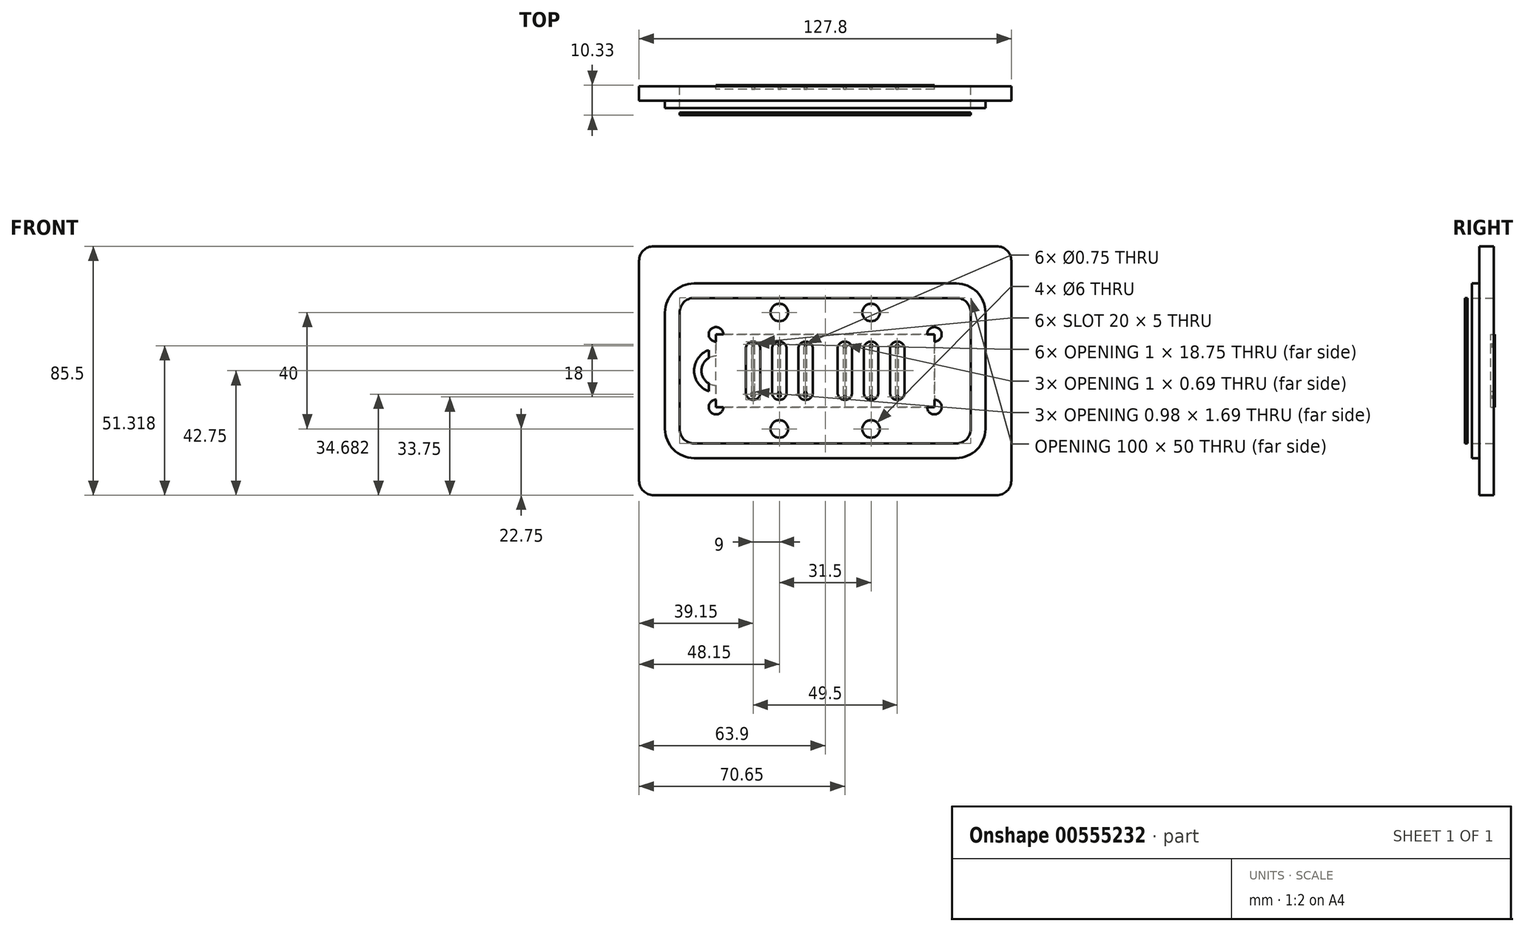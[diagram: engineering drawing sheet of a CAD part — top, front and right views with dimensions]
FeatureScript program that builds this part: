
annotation { "Feature Type Name" : "Feature", "Feature Type Description" : "" }
export const myFeature = defineFeature(function(context is Context, id is Id, definition is map)
    precondition{}
    {
        {
            var Q0;
            Q0=qCreatedBy(makeId("Front.planeOp"),FACE);
            var sketch = newSketch(context, id + "F0", { "sketchPlane" : qUnion([Q0])});
            skLineSegment(sketch, "E0.bottom", {"start": v(-58.9, 42.75) * mm, "end": v(58.9, 42.75) * mm});
            skLineSegment(sketch, "E0.top", {"start": v(-58.9, -42.75) * mm, "end": v(58.9, -42.75) * mm});
            skLineSegment(sketch, "E0.left", {"start": v(-63.9, 37.75) * mm, "end": v(-63.9, -37.75) * mm});
            skLineSegment(sketch, "E0.right", {"start": v(63.9, 37.75) * mm, "end": v(63.9, -37.75) * mm});
            skLineSegment(sketch, "E1.bottom", {"start": v(-37.5, 12.5) * mm, "end": v(37.5, 12.5) * mm});
            skLineSegment(sketch, "E1.top", {"start": v(-37.5, -12.5) * mm, "end": v(37.5, -12.5) * mm});
            skLineSegment(sketch, "E1.left", {"start": v(-37.5, 12.5) * mm, "end": v(-37.5, -12.5) * mm});
            skLineSegment(sketch, "E1.right", {"start": v(37.5, 12.5) * mm, "end": v(37.5, -12.5) * mm});
            skPoint(sketch, "E1.middle", {"position": v(0, 0) * mm});
            skPoint(sketch, "E2.visualSharp", {"position": v(-63.9, 42.75) * mm});
            skArc(sketch, "E2.filletArc", {"start": v(-58.9, 42.75) * mm, "mid": v(-62.44, 41.29) * mm, "end": v(-63.9, 37.75) * mm});
            skPoint(sketch, "E3.visualSharp", {"position": v(63.9, 42.75) * mm});
            skArc(sketch, "E3.filletArc", {"start": v(63.9, 37.75) * mm, "mid": v(62.44, 41.29) * mm, "end": v(58.9, 42.75) * mm});
            skPoint(sketch, "E4.visualSharp", {"position": v(63.9, -42.75) * mm});
            skArc(sketch, "E4.filletArc", {"start": v(58.9, -42.75) * mm, "mid": v(62.44, -41.29) * mm, "end": v(63.9, -37.75) * mm});
            skPoint(sketch, "E5.visualSharp", {"position": v(-63.9, -42.75) * mm});
            skArc(sketch, "E5.filletArc", {"start": v(-63.9, -37.75) * mm, "mid": v(-62.44, -41.29) * mm, "end": v(-58.9, -42.75) * mm});
            skCircle(sketch, "E6", {"center": v(-6.75, 9) * mm, "radius": 3.18 * mm});
            skCircle(sketch, "E7", {"center": v(-15.75, 9) * mm, "radius": 3.18 * mm});
            skCircle(sketch, "E8", {"center": v(-24.75, 9) * mm, "radius": 3.18 * mm});
            skCircle(sketch, "E9", {"center": v(6.75, 9) * mm, "radius": 3.18 * mm});
            skCircle(sketch, "E10", {"center": v(15.75, 9) * mm, "radius": 3.18 * mm});
            skCircle(sketch, "E11", {"center": v(24.75, 9) * mm, "radius": 3.18 * mm});
            skLineSegment(sketch, "E12.bottom", {"start": v(24.75, -10) * mm, "end": v(24.75, -10) * mm});
            skLineSegment(sketch, "E12.top", {"start": v(24.75, 10) * mm, "end": v(24.75, 10) * mm});
            skLineSegment(sketch, "E12.left", {"start": v(27.25, -7.5) * mm, "end": v(27.25, 7.5) * mm});
            skLineSegment(sketch, "E12.right", {"start": v(22.25, -7.5) * mm, "end": v(22.25, 7.5) * mm});
            skLineSegment(sketch, "E13.bottom", {"start": v(15.75, -10) * mm, "end": v(15.75, -10) * mm});
            skLineSegment(sketch, "E13.top", {"start": v(15.75, 10) * mm, "end": v(15.75, 10) * mm});
            skLineSegment(sketch, "E13.left", {"start": v(18.25, -7.5) * mm, "end": v(18.25, 7.5) * mm});
            skLineSegment(sketch, "E13.right", {"start": v(13.25, -7.5) * mm, "end": v(13.25, 7.5) * mm});
            skLineSegment(sketch, "E14.bottom", {"start": v(6.75, -10) * mm, "end": v(6.75, -10) * mm});
            skLineSegment(sketch, "E14.top", {"start": v(6.75, 10) * mm, "end": v(6.75, 10) * mm});
            skLineSegment(sketch, "E14.left", {"start": v(9.25, -7.5) * mm, "end": v(9.25, 7.5) * mm});
            skLineSegment(sketch, "E14.right", {"start": v(4.25, -7.5) * mm, "end": v(4.25, 7.5) * mm});
            skLineSegment(sketch, "E15.bottom", {"start": v(-6.75, -10) * mm, "end": v(-6.75, -10) * mm});
            skLineSegment(sketch, "E15.top", {"start": v(-6.75, 10) * mm, "end": v(-6.75, 10) * mm});
            skLineSegment(sketch, "E15.left", {"start": v(-4.25, -7.5) * mm, "end": v(-4.25, 7.5) * mm});
            skLineSegment(sketch, "E15.right", {"start": v(-9.25, -7.5) * mm, "end": v(-9.25, 7.5) * mm});
            skLineSegment(sketch, "E16.bottom", {"start": v(-15.75, -10) * mm, "end": v(-15.75, -10) * mm});
            skLineSegment(sketch, "E16.top", {"start": v(-15.75, 10) * mm, "end": v(-15.75, 10) * mm});
            skLineSegment(sketch, "E16.left", {"start": v(-13.25, -7.5) * mm, "end": v(-13.25, 7.5) * mm});
            skLineSegment(sketch, "E16.right", {"start": v(-18.25, -7.5) * mm, "end": v(-18.25, 7.5) * mm});
            skLineSegment(sketch, "E17.bottom", {"start": v(-24.75, -10) * mm, "end": v(-24.75, -10) * mm});
            skLineSegment(sketch, "E17.top", {"start": v(-24.75, 10) * mm, "end": v(-24.75, 10) * mm});
            skLineSegment(sketch, "E17.left", {"start": v(-22.25, -7.5) * mm, "end": v(-22.25, 7.5) * mm});
            skLineSegment(sketch, "E17.right", {"start": v(-27.25, -7.5) * mm, "end": v(-27.25, 7.5) * mm});
            skCircle(sketch, "E18", {"center": v(24.75, -9) * mm, "radius": 3.18 * mm});
            skPoint(sketch, "E19", {"position": v(24.75, -10) * mm});
            skCircle(sketch, "E20", {"center": v(15.75, -9) * mm, "radius": 3.18 * mm});
            skPoint(sketch, "E21", {"position": v(15.75, -10) * mm});
            skCircle(sketch, "E22", {"center": v(6.75, -9) * mm, "radius": 3.18 * mm});
            skPoint(sketch, "E23", {"position": v(6.75, -10) * mm});
            skCircle(sketch, "E24", {"center": v(-6.75, -9) * mm, "radius": 3.18 * mm});
            skPoint(sketch, "E25", {"position": v(-6.75, -10) * mm});
            skCircle(sketch, "E26", {"center": v(-15.75, -9) * mm, "radius": 3.18 * mm});
            skPoint(sketch, "E27", {"position": v(-15.75, -10) * mm});
            skCircle(sketch, "E28", {"center": v(-24.75, -9) * mm, "radius": 3.18 * mm});
            skPoint(sketch, "E29", {"position": v(-24.75, -10) * mm});
            skPoint(sketch, "E30.visualSharp", {"position": v(-27.25, 10) * mm});
            skArc(sketch, "E30.filletArc", {"start": v(-24.75, 10) * mm, "mid": v(-26.52, 9.27) * mm, "end": v(-27.25, 7.5) * mm});
            skPoint(sketch, "E31.visualSharp", {"position": v(-22.25, 10) * mm});
            skArc(sketch, "E31.filletArc", {"start": v(-22.25, 7.5) * mm, "mid": v(-22.98, 9.27) * mm, "end": v(-24.75, 10) * mm});
            skPoint(sketch, "E32.visualSharp", {"position": v(-22.25, -10) * mm});
            skArc(sketch, "E32.filletArc", {"start": v(-24.75, -10) * mm, "mid": v(-22.98, -9.27) * mm, "end": v(-22.25, -7.5) * mm});
            skPoint(sketch, "E33.visualSharp", {"position": v(-27.25, -10) * mm});
            skArc(sketch, "E33.filletArc", {"start": v(-27.25, -7.5) * mm, "mid": v(-26.52, -9.27) * mm, "end": v(-24.75, -10) * mm});
            skPoint(sketch, "E34.visualSharp", {"position": v(-18.25, -10) * mm});
            skArc(sketch, "E34.filletArc", {"start": v(-18.25, -7.5) * mm, "mid": v(-17.52, -9.27) * mm, "end": v(-15.75, -10) * mm});
            skPoint(sketch, "E35.visualSharp", {"position": v(-18.25, 10) * mm});
            skArc(sketch, "E35.filletArc", {"start": v(-15.75, 10) * mm, "mid": v(-17.52, 9.27) * mm, "end": v(-18.25, 7.5) * mm});
            skPoint(sketch, "E36.visualSharp", {"position": v(-13.25, 10) * mm});
            skArc(sketch, "E36.filletArc", {"start": v(-13.25, 7.5) * mm, "mid": v(-13.98, 9.27) * mm, "end": v(-15.75, 10) * mm});
            skPoint(sketch, "E37.visualSharp", {"position": v(-13.25, -10) * mm});
            skArc(sketch, "E37.filletArc", {"start": v(-15.75, -10) * mm, "mid": v(-13.98, -9.27) * mm, "end": v(-13.25, -7.5) * mm});
            skPoint(sketch, "E38.visualSharp", {"position": v(-9.25, -10) * mm});
            skArc(sketch, "E38.filletArc", {"start": v(-9.25, -7.5) * mm, "mid": v(-8.52, -9.27) * mm, "end": v(-6.75, -10) * mm});
            skPoint(sketch, "E39.visualSharp", {"position": v(-4.25, -10) * mm});
            skArc(sketch, "E39.filletArc", {"start": v(-6.75, -10) * mm, "mid": v(-4.98, -9.27) * mm, "end": v(-4.25, -7.5) * mm});
            skPoint(sketch, "E40.visualSharp", {"position": v(-9.25, 10) * mm});
            skArc(sketch, "E40.filletArc", {"start": v(-6.75, 10) * mm, "mid": v(-8.52, 9.27) * mm, "end": v(-9.25, 7.5) * mm});
            skPoint(sketch, "E41.visualSharp", {"position": v(-4.25, 10) * mm});
            skArc(sketch, "E41.filletArc", {"start": v(-4.25, 7.5) * mm, "mid": v(-4.98, 9.27) * mm, "end": v(-6.75, 10) * mm});
            skPoint(sketch, "E42.visualSharp", {"position": v(4.25, -10) * mm});
            skArc(sketch, "E42.filletArc", {"start": v(4.25, -7.5) * mm, "mid": v(4.98, -9.27) * mm, "end": v(6.75, -10) * mm});
            skPoint(sketch, "E43.visualSharp", {"position": v(9.25, -10) * mm});
            skArc(sketch, "E43.filletArc", {"start": v(6.75, -10) * mm, "mid": v(8.52, -9.27) * mm, "end": v(9.25, -7.5) * mm});
            skPoint(sketch, "E44.visualSharp", {"position": v(13.25, -10) * mm});
            skArc(sketch, "E44.filletArc", {"start": v(13.25, -7.5) * mm, "mid": v(13.98, -9.27) * mm, "end": v(15.75, -10) * mm});
            skPoint(sketch, "E45.visualSharp", {"position": v(18.25, -10) * mm});
            skArc(sketch, "E45.filletArc", {"start": v(15.75, -10) * mm, "mid": v(17.52, -9.27) * mm, "end": v(18.25, -7.5) * mm});
            skPoint(sketch, "E46.visualSharp", {"position": v(22.25, -10) * mm});
            skArc(sketch, "E46.filletArc", {"start": v(22.25, -7.5) * mm, "mid": v(22.98, -9.27) * mm, "end": v(24.75, -10) * mm});
            skPoint(sketch, "E47.visualSharp", {"position": v(27.25, -10) * mm});
            skArc(sketch, "E47.filletArc", {"start": v(24.75, -10) * mm, "mid": v(26.52, -9.27) * mm, "end": v(27.25, -7.5) * mm});
            skPoint(sketch, "E48.visualSharp", {"position": v(27.25, 10) * mm});
            skArc(sketch, "E48.filletArc", {"start": v(27.25, 7.5) * mm, "mid": v(26.52, 9.27) * mm, "end": v(24.75, 10) * mm});
            skPoint(sketch, "E49.visualSharp", {"position": v(22.25, 10) * mm});
            skArc(sketch, "E49.filletArc", {"start": v(24.75, 10) * mm, "mid": v(22.98, 9.27) * mm, "end": v(22.25, 7.5) * mm});
            skPoint(sketch, "E50.visualSharp", {"position": v(18.25, 10) * mm});
            skArc(sketch, "E50.filletArc", {"start": v(18.25, 7.5) * mm, "mid": v(17.52, 9.27) * mm, "end": v(15.75, 10) * mm});
            skPoint(sketch, "E51.visualSharp", {"position": v(13.25, 10) * mm});
            skArc(sketch, "E51.filletArc", {"start": v(15.75, 10) * mm, "mid": v(13.98, 9.27) * mm, "end": v(13.25, 7.5) * mm});
            skPoint(sketch, "E52.visualSharp", {"position": v(9.25, 10) * mm});
            skArc(sketch, "E52.filletArc", {"start": v(9.25, 7.5) * mm, "mid": v(8.52, 9.27) * mm, "end": v(6.75, 10) * mm});
            skPoint(sketch, "E53.visualSharp", {"position": v(4.25, 10) * mm});
            skArc(sketch, "E53.filletArc", {"start": v(6.75, 10) * mm, "mid": v(4.98, 9.27) * mm, "end": v(4.25, 7.5) * mm});
            skCircle(sketch, "E54", {"center": v(-37.5, 0) * mm, "radius": 5 * mm});
            skLineSegment(sketch, "E55.bottom", {"start": v(-37.5, 15) * mm, "end": v(37.5, 15) * mm});
            skLineSegment(sketch, "E55.top", {"start": v(-37.5, -15) * mm, "end": v(37.5, -15) * mm});
            skLineSegment(sketch, "E55.left", {"start": v(-40, 12.5) * mm, "end": v(-40, -12.5) * mm});
            skLineSegment(sketch, "E55.right", {"start": v(40, 12.5) * mm, "end": v(40, -12.5) * mm});
            skArc(sketch, "E56", {"start": v(-40, -7.07) * mm, "mid": v(-45, 0) * mm, "end": v(-40, 7.07) * mm});
            skArc(sketch, "E57", {"start": v(-37.5, 10) * mm, "mid": v(-39.27, 14.27) * mm, "end": v(-35, 12.5) * mm});
            skArc(sketch, "E58", {"start": v(35, 12.5) * mm, "mid": v(39.27, 14.27) * mm, "end": v(37.5, 10) * mm});
            skArc(sketch, "E59", {"start": v(37.5, -10) * mm, "mid": v(39.27, -14.27) * mm, "end": v(35, -12.5) * mm});
            skArc(sketch, "E60", {"start": v(-35, -12.5) * mm, "mid": v(-39.27, -14.27) * mm, "end": v(-37.5, -10) * mm});
            skPoint(sketch, "E61.visualSharp", {"position": v(-40, 15) * mm});
            skArc(sketch, "E61.filletArc", {"start": v(-37.5, 15) * mm, "mid": v(-39.27, 14.27) * mm, "end": v(-40, 12.5) * mm});
            skPoint(sketch, "E62.visualSharp", {"position": v(-40, -15) * mm});
            skArc(sketch, "E62.filletArc", {"start": v(-40, -12.5) * mm, "mid": v(-39.27, -14.27) * mm, "end": v(-37.5, -15) * mm});
            skPoint(sketch, "E63.visualSharp", {"position": v(40, -15) * mm});
            skArc(sketch, "E63.filletArc", {"start": v(37.5, -15) * mm, "mid": v(39.27, -14.27) * mm, "end": v(40, -12.5) * mm});
            skPoint(sketch, "E64.visualSharp", {"position": v(40, 15) * mm});
            skArc(sketch, "E64.filletArc", {"start": v(40, 12.5) * mm, "mid": v(39.27, 14.27) * mm, "end": v(37.5, 15) * mm});
            skCircle(sketch, "E65", {"center": v(-15.75, 20) * mm, "radius": 3 * mm});
            skCircle(sketch, "E66", {"center": v(15.75, 20) * mm, "radius": 3 * mm});
            skCircle(sketch, "E67", {"center": v(15.75, -20) * mm, "radius": 3 * mm});
            skCircle(sketch, "E68", {"center": v(-15.75, -20) * mm, "radius": 3 * mm});
            skCircle(sketch, "E69", {"center": v(-15.75, -9) * mm, "radius": 0.38 * mm});
            skCircle(sketch, "E70", {"center": v(-6.75, -9) * mm, "radius": 0.38 * mm});
            skCircle(sketch, "E71", {"center": v(6.75, -9) * mm, "radius": 0.38 * mm});
            skCircle(sketch, "E72", {"center": v(15.75, -9) * mm, "radius": 0.38 * mm});
            skCircle(sketch, "E73", {"center": v(24.75, -9) * mm, "radius": 0.38 * mm});
            skCircle(sketch, "E74", {"center": v(24.75, 9) * mm, "radius": 0.38 * mm});
            skCircle(sketch, "E75", {"center": v(15.75, 9) * mm, "radius": 0.38 * mm});
            skCircle(sketch, "E76", {"center": v(6.75, 9) * mm, "radius": 0.38 * mm});
            skCircle(sketch, "E77", {"center": v(-6.75, 9) * mm, "radius": 0.38 * mm});
            skCircle(sketch, "E78", {"center": v(-15.75, 9) * mm, "radius": 0.38 * mm});
            skCircle(sketch, "E79", {"center": v(-24.75, 9) * mm, "radius": 0.38 * mm});
            skCircle(sketch, "E80", {"center": v(-24.75, -9) * mm, "radius": 0.38 * mm});
            skLineSegment(sketch, "E81.bottom", {"start": v(-45, 25) * mm, "end": v(45, 25) * mm});
            skLineSegment(sketch, "E81.top", {"start": v(-45, -25) * mm, "end": v(45, -25) * mm});
            skLineSegment(sketch, "E81.left", {"start": v(-50, 20) * mm, "end": v(-50, -20) * mm});
            skLineSegment(sketch, "E81.right", {"start": v(50, 20) * mm, "end": v(50, -20) * mm});
            skPoint(sketch, "E82.visualSharp", {"position": v(-50, -25) * mm});
            skArc(sketch, "E82.filletArc", {"start": v(-50, -20) * mm, "mid": v(-48.54, -23.54) * mm, "end": v(-45, -25) * mm});
            skPoint(sketch, "E83.visualSharp", {"position": v(50, -25) * mm});
            skArc(sketch, "E83.filletArc", {"start": v(45, -25) * mm, "mid": v(48.54, -23.54) * mm, "end": v(50, -20) * mm});
            skPoint(sketch, "E84.visualSharp", {"position": v(50, 25) * mm});
            skArc(sketch, "E84.filletArc", {"start": v(50, 20) * mm, "mid": v(48.54, 23.54) * mm, "end": v(45, 25) * mm});
            skPoint(sketch, "E85.visualSharp", {"position": v(-50, 25) * mm});
            skArc(sketch, "E85.filletArc", {"start": v(-45, 25) * mm, "mid": v(-48.54, 23.54) * mm, "end": v(-50, 20) * mm});
            skLineSegment(sketch, "E86.bottom", {"start": v(-45, -30) * mm, "end": v(45, -30) * mm});
            skLineSegment(sketch, "E86.top", {"start": v(-45, 30) * mm, "end": v(45, 30) * mm});
            skLineSegment(sketch, "E86.left", {"start": v(-55, -20) * mm, "end": v(-55, 20) * mm});
            skLineSegment(sketch, "E86.right", {"start": v(55, -20) * mm, "end": v(55, 20) * mm});
            skPoint(sketch, "E87.visualSharp", {"position": v(-55, -30) * mm});
            skArc(sketch, "E87.filletArc", {"start": v(-55, -20) * mm, "mid": v(-52.07, -27.07) * mm, "end": v(-45, -30) * mm});
            skPoint(sketch, "E88.visualSharp", {"position": v(55, -30) * mm});
            skArc(sketch, "E88.filletArc", {"start": v(45, -30) * mm, "mid": v(52.07, -27.07) * mm, "end": v(55, -20) * mm});
            skPoint(sketch, "E89.visualSharp", {"position": v(55, 30) * mm});
            skArc(sketch, "E89.filletArc", {"start": v(55, 20) * mm, "mid": v(52.07, 27.07) * mm, "end": v(45, 30) * mm});
            skPoint(sketch, "E90.visualSharp", {"position": v(-55, 30) * mm});
            skArc(sketch, "E90.filletArc", {"start": v(-45, 30) * mm, "mid": v(-52.07, 27.07) * mm, "end": v(-55, 20) * mm});
            skSolve(sketch);
        }
        {
            var Q0;
            Q0=makeQuery(id+"F0.imprint","IMPRINT",FACE,{"disambiguationData":[TD([[makeQuery(id+"F0.imprint","IMPRINT",EDGE,{"derivedFrom":sQuery(id+"F0.wireOp",EDGE,"E0.bottom")}),-1.0]])]});
            extrude(context, id + "F1", {"entities" : qUnion([Q0]), "depth" : 5 * mm, "offsetDistance" : 25 * mm});
        }
        {
            var Q0;
            Q0=makeQuery(id+"F0.imprint","IMPRINT",FACE,{"disambiguationData":[TD([[makeQuery(id+"F0.imprint","IMPRINT",EDGE,{"derivedFrom":sQuery(id+"F0.wireOp",EDGE,"E81.bottom")}),1.0]])]});
            extrude(context, id + "F2", {"entities" : qUnion([Q0]), "operationType" : NewBodyOperationType.ADD, "depth" : 2.5 * mm, "offsetDistance" : 25 * mm});
        }
        {
            var Q0;
            Q0=makeQuery(id+"F0.imprint","IMPRINT",FACE,{"disambiguationData":[TD([[makeQuery(id+"F0.imprint","IMPRINT",EDGE,{"derivedFrom":sQuery(id+"F0.wireOp",EDGE,"E81.bottom")}),1.0]])]});
            extrude(context, id + "F3", {"entities" : qUnion([Q0]), "depth" : 7.5 * mm, "offsetDistance" : 25 * mm});
        }
        {
            var Q0;
            Q0=makeQuery(id+"F0.imprint","IMPRINT",FACE,{"disambiguationData":[TD([[makeQuery(id+"F0.imprint","IMPRINT",EDGE,{"derivedFrom":sQuery(id+"F0.wireOp",EDGE,"E55.bottom")}),1.0]])]});
            var Q1;
            {var subQ0=sQuery(id+"F0.wireOp",EDGE,"E14.left");var subQ1=sQuery(id+"F0.wireOp",EDGE,"E9");var subQ2=makeQuery(id+"F0.imprint","INTERSECT",VERTEX,{"derivedFrom":[subQ1,subQ0]});Q1=makeQuery(id+"F0.imprint","IMPRINT",FACE,{"disambiguationData":[TD([[makeQuery(id+"F0.imprint","IMPRINT",EDGE,{"disambiguationData":[TD([[subQ2,1.0]])],"derivedFrom":subQ1}),-1.0]])]});}
            var Q2;
            {var subQ0=sQuery(id+"F0.wireOp",EDGE,"E13.left");var subQ1=sQuery(id+"F0.wireOp",EDGE,"E10");var subQ2=makeQuery(id+"F0.imprint","INTERSECT",VERTEX,{"derivedFrom":[subQ1,subQ0]});Q2=makeQuery(id+"F0.imprint","IMPRINT",FACE,{"disambiguationData":[TD([[makeQuery(id+"F0.imprint","IMPRINT",EDGE,{"disambiguationData":[TD([[subQ2,1.0]])],"derivedFrom":subQ1}),-1.0]])]});}
            var Q3;
            {var subQ0=sQuery(id+"F0.wireOp",EDGE,"E15.left");var subQ1=sQuery(id+"F0.wireOp",EDGE,"E6");var subQ2=makeQuery(id+"F0.imprint","INTERSECT",VERTEX,{"derivedFrom":[subQ1,subQ0]});Q3=makeQuery(id+"F0.imprint","IMPRINT",FACE,{"disambiguationData":[TD([[makeQuery(id+"F0.imprint","IMPRINT",EDGE,{"disambiguationData":[TD([[subQ2,1.0]])],"derivedFrom":subQ1}),-1.0]])]});}
            var Q4;
            {var subQ0=sQuery(id+"F0.wireOp",EDGE,"E48.filletArc");Q4=makeQuery(id+"F0.imprint","IMPRINT",FACE,{"disambiguationData":[TD([[makeQuery(id+"F0.imprint","IMPRINT",EDGE,{"derivedFrom":subQ0}),1.0]])]});}
            var Q5;
            {var subQ5=sQuery(id+"F0.wireOp",EDGE,"E38.filletArc");Q5=makeQuery(id+"F0.imprint","IMPRINT",FACE,{"disambiguationData":[TD([[makeQuery(id+"F0.imprint","IMPRINT",EDGE,{"derivedFrom":subQ5}),1.0]])]});}
            var Q6;
            {var subQ4=sQuery(id+"F0.wireOp",EDGE,"E50.filletArc");Q6=makeQuery(id+"F0.imprint","IMPRINT",FACE,{"disambiguationData":[TD([[makeQuery(id+"F0.imprint","IMPRINT",EDGE,{"derivedFrom":subQ4}),-1.0]])]});}
            var Q7;
            {var subQ0=sQuery(id+"F0.wireOp",EDGE,"E38.filletArc");Q7=makeQuery(id+"F0.imprint","IMPRINT",FACE,{"disambiguationData":[TD([[makeQuery(id+"F0.imprint","IMPRINT",EDGE,{"derivedFrom":subQ0}),-1.0]])]});}
            var Q8;
            {var subQ0=sQuery(id+"F0.wireOp",EDGE,"E46.filletArc");Q8=makeQuery(id+"F0.imprint","IMPRINT",FACE,{"disambiguationData":[TD([[makeQuery(id+"F0.imprint","IMPRINT",EDGE,{"derivedFrom":subQ0}),1.0]])]});}
            var Q9;
            {var subQ0=sQuery(id+"F0.wireOp",EDGE,"E62.filletArc");Q9=makeQuery(id+"F0.imprint","IMPRINT",FACE,{"disambiguationData":[TD([[makeQuery(id+"F0.imprint","IMPRINT",EDGE,{"derivedFrom":subQ0}),1.0]])]});}
            var Q10;
            {var subQ0=sQuery(id+"F0.wireOp",EDGE,"E44.filletArc");Q10=makeQuery(id+"F0.imprint","IMPRINT",FACE,{"disambiguationData":[TD([[makeQuery(id+"F0.imprint","IMPRINT",EDGE,{"derivedFrom":subQ0}),-1.0]])]});}
            var Q11;
            {var subQ0=sQuery(id+"F0.wireOp",EDGE,"E52.filletArc");Q11=makeQuery(id+"F0.imprint","IMPRINT",FACE,{"disambiguationData":[TD([[makeQuery(id+"F0.imprint","IMPRINT",EDGE,{"derivedFrom":subQ0}),1.0]])]});}
            var Q12;
            {var subQ0=sQuery(id+"F0.wireOp",EDGE,"E34.filletArc");Q12=makeQuery(id+"F0.imprint","IMPRINT",FACE,{"disambiguationData":[TD([[makeQuery(id+"F0.imprint","IMPRINT",EDGE,{"derivedFrom":subQ0}),1.0]])]});}
            var Q13;
            {var subQ5=sQuery(id+"F0.wireOp",EDGE,"E55.right");Q13=makeQuery(id+"F0.imprint","IMPRINT",FACE,{"disambiguationData":[TD([[makeQuery(id+"F0.imprint","IMPRINT",EDGE,{"derivedFrom":subQ5}),-1.0]])]});}
            var Q14;
            {var subQ30=sQuery(id+"F0.wireOp",EDGE,"E1.bottom");var subQ35=sQuery(id+"F0.wireOp",EDGE,"E1.left");var subQ56=makeQuery(id+"F0.imprint","INTERSECT",VERTEX,{"derivedFrom":[subQ30,subQ35]});Q14=makeQuery(id+"F0.imprint","IMPRINT",FACE,{"disambiguationData":[TD([[makeQuery(id+"F0.imprint","IMPRINT",EDGE,{"disambiguationData":[TD([[subQ56,-1.0]])],"derivedFrom":subQ30}),-1.0]])]});}
            var Q15;
            {var subQ0=sQuery(id+"F0.wireOp",EDGE,"E54");var subQ1=sQuery(id+"F0.wireOp",EDGE,"E1.left");var subQ2=makeQuery(id+"F0.imprint","INTERSECT",VERTEX,{"disambiguationData":[OD(0.0)],"derivedFrom":[subQ1,subQ0]});Q15=makeQuery(id+"F0.imprint","IMPRINT",FACE,{"disambiguationData":[TD([[makeQuery(id+"F0.imprint","IMPRINT",EDGE,{"disambiguationData":[TD([[subQ2,-1.0]])],"derivedFrom":subQ1}),-1.0]])]});}
            var Q16;
            {var subQ0=sQuery(id+"F0.wireOp",EDGE,"E12.left");var subQ1=sQuery(id+"F0.wireOp",EDGE,"E11");var subQ2=makeQuery(id+"F0.imprint","INTERSECT",VERTEX,{"derivedFrom":[subQ1,subQ0]});Q16=makeQuery(id+"F0.imprint","IMPRINT",FACE,{"disambiguationData":[TD([[makeQuery(id+"F0.imprint","IMPRINT",EDGE,{"disambiguationData":[TD([[subQ2,1.0]])],"derivedFrom":subQ1}),-1.0]])]});}
            var Q17;
            {var subQ0=sQuery(id+"F0.wireOp",EDGE,"E46.filletArc");Q17=makeQuery(id+"F0.imprint","IMPRINT",FACE,{"disambiguationData":[TD([[makeQuery(id+"F0.imprint","IMPRINT",EDGE,{"derivedFrom":subQ0}),-1.0]])]});}
            var Q18;
            {var subQ5=sQuery(id+"F0.wireOp",EDGE,"E42.filletArc");Q18=makeQuery(id+"F0.imprint","IMPRINT",FACE,{"disambiguationData":[TD([[makeQuery(id+"F0.imprint","IMPRINT",EDGE,{"derivedFrom":subQ5}),-1.0]])]});}
            var Q19;
            {var subQ5=sQuery(id+"F0.wireOp",EDGE,"E55.top");Q19=makeQuery(id+"F0.imprint","IMPRINT",FACE,{"disambiguationData":[TD([[makeQuery(id+"F0.imprint","IMPRINT",EDGE,{"derivedFrom":subQ5}),1.0]])]});}
            var Q20;
            {var subQ0=sQuery(id+"F0.wireOp",EDGE,"E50.filletArc");Q20=makeQuery(id+"F0.imprint","IMPRINT",FACE,{"disambiguationData":[TD([[makeQuery(id+"F0.imprint","IMPRINT",EDGE,{"derivedFrom":subQ0}),1.0]])]});}
            var Q21;
            {var subQ0=sQuery(id+"F0.wireOp",EDGE,"E55.left");var subQ1=sQuery(id+"F0.wireOp",EDGE,"E54");var subQ2=makeQuery(id+"F0.imprint","INTERSECT",VERTEX,{"disambiguationData":[OD(0.0)],"derivedFrom":[subQ1,subQ0]});Q21=makeQuery(id+"F0.imprint","IMPRINT",FACE,{"disambiguationData":[TD([[makeQuery(id+"F0.imprint","IMPRINT",EDGE,{"disambiguationData":[TD([[subQ2,-1.0]])],"derivedFrom":subQ1}),1.0]])]});}
            var Q22;
            {var subQ0=sQuery(id+"F0.wireOp",EDGE,"E42.filletArc");Q22=makeQuery(id+"F0.imprint","IMPRINT",FACE,{"disambiguationData":[TD([[makeQuery(id+"F0.imprint","IMPRINT",EDGE,{"derivedFrom":subQ0}),1.0]])]});}
            var Q23;
            {var subQ6=sQuery(id+"F0.wireOp",EDGE,"E32.filletArc");Q23=makeQuery(id+"F0.imprint","IMPRINT",FACE,{"disambiguationData":[TD([[makeQuery(id+"F0.imprint","IMPRINT",EDGE,{"derivedFrom":subQ6}),-1.0]])]});}
            var Q24;
            {var subQ0=sQuery(id+"F0.wireOp",EDGE,"E16.left");var subQ1=sQuery(id+"F0.wireOp",EDGE,"E7");var subQ2=makeQuery(id+"F0.imprint","INTERSECT",VERTEX,{"derivedFrom":[subQ1,subQ0]});Q24=makeQuery(id+"F0.imprint","IMPRINT",FACE,{"disambiguationData":[TD([[makeQuery(id+"F0.imprint","IMPRINT",EDGE,{"disambiguationData":[TD([[subQ2,1.0]])],"derivedFrom":subQ1}),-1.0]])]});}
            var Q25;
            {var subQ0=sQuery(id+"F0.wireOp",EDGE,"E17.left");var subQ1=sQuery(id+"F0.wireOp",EDGE,"E8");var subQ2=makeQuery(id+"F0.imprint","INTERSECT",VERTEX,{"derivedFrom":[subQ1,subQ0]});Q25=makeQuery(id+"F0.imprint","IMPRINT",FACE,{"disambiguationData":[TD([[makeQuery(id+"F0.imprint","IMPRINT",EDGE,{"disambiguationData":[TD([[subQ2,1.0]])],"derivedFrom":subQ1}),-1.0]])]});}
            var Q26;
            {var subQ4=sQuery(id+"F0.wireOp",EDGE,"E57");var subQ6=sQuery(id+"F0.wireOp",EDGE,"E1.left");var subQ8=makeQuery(id+"F0.imprint","INTERSECT",VERTEX,{"derivedFrom":[subQ6,subQ4]});Q26=makeQuery(id+"F0.imprint","IMPRINT",FACE,{"disambiguationData":[TD([[makeQuery(id+"F0.imprint","IMPRINT",EDGE,{"disambiguationData":[TD([[subQ8,-1.0]])],"derivedFrom":subQ6}),-1.0]])]});}
            var Q27;
            {var subQ0=sQuery(id+"F0.wireOp",EDGE,"E30.filletArc");Q27=makeQuery(id+"F0.imprint","IMPRINT",FACE,{"disambiguationData":[TD([[makeQuery(id+"F0.imprint","IMPRINT",EDGE,{"derivedFrom":subQ0}),-1.0]])]});}
            var Q28;
            {var subQ0=sQuery(id+"F0.wireOp",EDGE,"E60");var subQ6=sQuery(id+"F0.wireOp",EDGE,"E1.left");var subQ7=makeQuery(id+"F0.imprint","INTERSECT",VERTEX,{"derivedFrom":[subQ6,subQ0]});Q28=makeQuery(id+"F0.imprint","IMPRINT",FACE,{"disambiguationData":[TD([[makeQuery(id+"F0.imprint","IMPRINT",EDGE,{"disambiguationData":[TD([[subQ7,1.0]])],"derivedFrom":subQ6}),-1.0]])]});}
            var Q29;
            {var subQ5=sQuery(id+"F0.wireOp",EDGE,"E34.filletArc");Q29=makeQuery(id+"F0.imprint","IMPRINT",FACE,{"disambiguationData":[TD([[makeQuery(id+"F0.imprint","IMPRINT",EDGE,{"derivedFrom":subQ5}),-1.0]])]});}
            var Q30;
            {var subQ0=sQuery(id+"F0.wireOp",EDGE,"E30.filletArc");Q30=makeQuery(id+"F0.imprint","IMPRINT",FACE,{"disambiguationData":[TD([[makeQuery(id+"F0.imprint","IMPRINT",EDGE,{"derivedFrom":subQ0}),1.0]])]});}
            var Q31;
            {var subQ5=sQuery(id+"F0.wireOp",EDGE,"E55.bottom");Q31=makeQuery(id+"F0.imprint","IMPRINT",FACE,{"disambiguationData":[TD([[makeQuery(id+"F0.imprint","IMPRINT",EDGE,{"derivedFrom":subQ5}),-1.0]])]});}
            var Q32;
            {var subQ4=sQuery(id+"F0.wireOp",EDGE,"E56");Q32=makeQuery(id+"F0.imprint","IMPRINT",FACE,{"disambiguationData":[TD([[makeQuery(id+"F0.imprint","IMPRINT",EDGE,{"derivedFrom":subQ4}),-1.0]])]});}
            var Q33;
            {var subQ0=sQuery(id+"F0.wireOp",EDGE,"E35.filletArc");Q33=makeQuery(id+"F0.imprint","IMPRINT",FACE,{"disambiguationData":[TD([[makeQuery(id+"F0.imprint","IMPRINT",EDGE,{"derivedFrom":subQ0}),1.0]])]});}
            var Q34;
            {var subQ0=sQuery(id+"F0.wireOp",EDGE,"E35.filletArc");Q34=makeQuery(id+"F0.imprint","IMPRINT",FACE,{"disambiguationData":[TD([[makeQuery(id+"F0.imprint","IMPRINT",EDGE,{"derivedFrom":subQ0}),-1.0]])]});}
            var Q35;
            {var subQ6=sQuery(id+"F0.wireOp",EDGE,"E52.filletArc");Q35=makeQuery(id+"F0.imprint","IMPRINT",FACE,{"disambiguationData":[TD([[makeQuery(id+"F0.imprint","IMPRINT",EDGE,{"derivedFrom":subQ6}),-1.0]])]});}
            var Q36;
            {var subQ0=sQuery(id+"F0.wireOp",EDGE,"E64.filletArc");Q36=makeQuery(id+"F0.imprint","IMPRINT",FACE,{"disambiguationData":[TD([[makeQuery(id+"F0.imprint","IMPRINT",EDGE,{"derivedFrom":subQ0}),1.0]])]});}
            var Q37;
            {var subQ0=sQuery(id+"F0.wireOp",EDGE,"E44.filletArc");Q37=makeQuery(id+"F0.imprint","IMPRINT",FACE,{"disambiguationData":[TD([[makeQuery(id+"F0.imprint","IMPRINT",EDGE,{"derivedFrom":subQ0}),1.0]])]});}
            var Q38;
            {var subQ0=sQuery(id+"F0.wireOp",EDGE,"E40.filletArc");Q38=makeQuery(id+"F0.imprint","IMPRINT",FACE,{"disambiguationData":[TD([[makeQuery(id+"F0.imprint","IMPRINT",EDGE,{"derivedFrom":subQ0}),-1.0]])]});}
            var Q39;
            {var subQ6=sQuery(id+"F0.wireOp",EDGE,"E32.filletArc");Q39=makeQuery(id+"F0.imprint","IMPRINT",FACE,{"disambiguationData":[TD([[makeQuery(id+"F0.imprint","IMPRINT",EDGE,{"derivedFrom":subQ6}),1.0]])]});}
            var Q40;
            {var subQ4=sQuery(id+"F0.wireOp",EDGE,"E40.filletArc");Q40=makeQuery(id+"F0.imprint","IMPRINT",FACE,{"disambiguationData":[TD([[makeQuery(id+"F0.imprint","IMPRINT",EDGE,{"derivedFrom":subQ4}),1.0]])]});}
            var Q41;
            {var subQ0=sQuery(id+"F0.wireOp",EDGE,"E54");var subQ1=sQuery(id+"F0.wireOp",EDGE,"E1.left");var subQ2=makeQuery(id+"F0.imprint","INTERSECT",VERTEX,{"disambiguationData":[OD(0.0)],"derivedFrom":[subQ1,subQ0]});Q41=makeQuery(id+"F0.imprint","IMPRINT",FACE,{"disambiguationData":[TD([[makeQuery(id+"F0.imprint","IMPRINT",EDGE,{"disambiguationData":[TD([[subQ2,-1.0]])],"derivedFrom":subQ1}),1.0]])]});}
            var Q42;
            {var subQ0=sQuery(id+"F0.wireOp",EDGE,"E63.filletArc");Q42=makeQuery(id+"F0.imprint","IMPRINT",FACE,{"disambiguationData":[TD([[makeQuery(id+"F0.imprint","IMPRINT",EDGE,{"derivedFrom":subQ0}),1.0]])]});}
            var Q43;
            {var subQ0=sQuery(id+"F0.wireOp",EDGE,"E48.filletArc");Q43=makeQuery(id+"F0.imprint","IMPRINT",FACE,{"disambiguationData":[TD([[makeQuery(id+"F0.imprint","IMPRINT",EDGE,{"derivedFrom":subQ0}),-1.0]])]});}
            var Q44;
            {var subQ0=sQuery(id+"F0.wireOp",EDGE,"E61.filletArc");Q44=makeQuery(id+"F0.imprint","IMPRINT",FACE,{"disambiguationData":[TD([[makeQuery(id+"F0.imprint","IMPRINT",EDGE,{"derivedFrom":subQ0}),1.0]])]});}
            var Q45;
            Q45=makeQuery(id+"F0.imprint","IMPRINT",FACE,{"disambiguationData":[TD([[makeQuery(id+"F0.imprint","IMPRINT",EDGE,{"derivedFrom":sQuery(id+"F0.wireOp",EDGE,"E69")}),1.0]])]});
            var Q46;
            Q46=makeQuery(id+"F0.imprint","IMPRINT",FACE,{"disambiguationData":[TD([[makeQuery(id+"F0.imprint","IMPRINT",EDGE,{"derivedFrom":sQuery(id+"F0.wireOp",EDGE,"E72")}),1.0]])]});
            var Q47;
            Q47=makeQuery(id+"F0.imprint","IMPRINT",FACE,{"disambiguationData":[TD([[makeQuery(id+"F0.imprint","IMPRINT",EDGE,{"derivedFrom":sQuery(id+"F0.wireOp",EDGE,"E79")}),1.0]])]});
            var Q48;
            Q48=makeQuery(id+"F0.imprint","IMPRINT",FACE,{"disambiguationData":[TD([[makeQuery(id+"F0.imprint","IMPRINT",EDGE,{"derivedFrom":sQuery(id+"F0.wireOp",EDGE,"E78")}),1.0]])]});
            var Q49;
            Q49=makeQuery(id+"F0.imprint","IMPRINT",FACE,{"disambiguationData":[TD([[makeQuery(id+"F0.imprint","IMPRINT",EDGE,{"derivedFrom":sQuery(id+"F0.wireOp",EDGE,"E77")}),1.0]])]});
            var Q50;
            Q50=makeQuery(id+"F0.imprint","IMPRINT",FACE,{"disambiguationData":[TD([[makeQuery(id+"F0.imprint","IMPRINT",EDGE,{"derivedFrom":sQuery(id+"F0.wireOp",EDGE,"E76")}),1.0]])]});
            var Q51;
            Q51=makeQuery(id+"F0.imprint","IMPRINT",FACE,{"disambiguationData":[TD([[makeQuery(id+"F0.imprint","IMPRINT",EDGE,{"derivedFrom":sQuery(id+"F0.wireOp",EDGE,"E75")}),1.0]])]});
            var Q52;
            Q52=makeQuery(id+"F0.imprint","IMPRINT",FACE,{"disambiguationData":[TD([[makeQuery(id+"F0.imprint","IMPRINT",EDGE,{"derivedFrom":sQuery(id+"F0.wireOp",EDGE,"E70")}),1.0]])]});
            var Q53;
            Q53=makeQuery(id+"F0.imprint","IMPRINT",FACE,{"disambiguationData":[TD([[makeQuery(id+"F0.imprint","IMPRINT",EDGE,{"derivedFrom":sQuery(id+"F0.wireOp",EDGE,"E73")}),1.0]])]});
            var Q54;
            Q54=makeQuery(id+"F0.imprint","IMPRINT",FACE,{"disambiguationData":[TD([[makeQuery(id+"F0.imprint","IMPRINT",EDGE,{"derivedFrom":sQuery(id+"F0.wireOp",EDGE,"E74")}),1.0]])]});
            var Q55;
            Q55=makeQuery(id+"F0.imprint","IMPRINT",FACE,{"disambiguationData":[TD([[makeQuery(id+"F0.imprint","IMPRINT",EDGE,{"derivedFrom":sQuery(id+"F0.wireOp",EDGE,"E80")}),1.0]])]});
            var Q56;
            Q56=makeQuery(id+"F0.imprint","IMPRINT",FACE,{"disambiguationData":[TD([[makeQuery(id+"F0.imprint","IMPRINT",EDGE,{"derivedFrom":sQuery(id+"F0.wireOp",EDGE,"E71")}),1.0]])]});
            extrude(context, id + "F4", {"entities" : qUnion([Q0, Q1, Q2, Q3, Q4, Q5, Q6, Q7, Q8, Q9, Q10, Q11, Q12, Q13, Q14, Q15, Q16, Q17, Q18, Q19, Q20, Q21, Q22, Q23, Q24, Q25, Q26, Q27, Q28, Q29, Q30, Q31, Q32, Q33, Q34, Q35, Q36, Q37, Q38, Q39, Q40, Q41, Q42, Q43, Q44, Q45, Q46, Q47, Q48, Q49, Q50, Q51, Q52, Q53, Q54, Q55, Q56]), "operationType" : NewBodyOperationType.ADD, "depth" : 10 * mm, "offsetDistance" : 25 * mm});
        }
        {
            var Q0;
            {var subQ0=sQuery(id+"F0.wireOp",EDGE,"E14.left");var subQ1=sQuery(id+"F0.wireOp",EDGE,"E9");var subQ2=makeQuery(id+"F0.imprint","INTERSECT",VERTEX,{"derivedFrom":[subQ1,subQ0]});Q0=makeQuery(id+"F0.imprint","IMPRINT",FACE,{"disambiguationData":[TD([[makeQuery(id+"F0.imprint","IMPRINT",EDGE,{"disambiguationData":[TD([[subQ2,1.0]])],"derivedFrom":subQ1}),-1.0]])]});}
            var Q1;
            {var subQ0=sQuery(id+"F0.wireOp",EDGE,"E13.left");var subQ1=sQuery(id+"F0.wireOp",EDGE,"E10");var subQ2=makeQuery(id+"F0.imprint","INTERSECT",VERTEX,{"derivedFrom":[subQ1,subQ0]});Q1=makeQuery(id+"F0.imprint","IMPRINT",FACE,{"disambiguationData":[TD([[makeQuery(id+"F0.imprint","IMPRINT",EDGE,{"disambiguationData":[TD([[subQ2,1.0]])],"derivedFrom":subQ1}),-1.0]])]});}
            var Q2;
            {var subQ0=sQuery(id+"F0.wireOp",EDGE,"E15.left");var subQ1=sQuery(id+"F0.wireOp",EDGE,"E6");var subQ2=makeQuery(id+"F0.imprint","INTERSECT",VERTEX,{"derivedFrom":[subQ1,subQ0]});Q2=makeQuery(id+"F0.imprint","IMPRINT",FACE,{"disambiguationData":[TD([[makeQuery(id+"F0.imprint","IMPRINT",EDGE,{"disambiguationData":[TD([[subQ2,1.0]])],"derivedFrom":subQ1}),-1.0]])]});}
            var Q3;
            {var subQ0=sQuery(id+"F0.wireOp",EDGE,"E48.filletArc");Q3=makeQuery(id+"F0.imprint","IMPRINT",FACE,{"disambiguationData":[TD([[makeQuery(id+"F0.imprint","IMPRINT",EDGE,{"derivedFrom":subQ0}),1.0]])]});}
            var Q4;
            {var subQ5=sQuery(id+"F0.wireOp",EDGE,"E38.filletArc");Q4=makeQuery(id+"F0.imprint","IMPRINT",FACE,{"disambiguationData":[TD([[makeQuery(id+"F0.imprint","IMPRINT",EDGE,{"derivedFrom":subQ5}),1.0]])]});}
            var Q5;
            {var subQ4=sQuery(id+"F0.wireOp",EDGE,"E50.filletArc");Q5=makeQuery(id+"F0.imprint","IMPRINT",FACE,{"disambiguationData":[TD([[makeQuery(id+"F0.imprint","IMPRINT",EDGE,{"derivedFrom":subQ4}),-1.0]])]});}
            var Q6;
            {var subQ0=sQuery(id+"F0.wireOp",EDGE,"E38.filletArc");Q6=makeQuery(id+"F0.imprint","IMPRINT",FACE,{"disambiguationData":[TD([[makeQuery(id+"F0.imprint","IMPRINT",EDGE,{"derivedFrom":subQ0}),-1.0]])]});}
            var Q7;
            {var subQ0=sQuery(id+"F0.wireOp",EDGE,"E46.filletArc");Q7=makeQuery(id+"F0.imprint","IMPRINT",FACE,{"disambiguationData":[TD([[makeQuery(id+"F0.imprint","IMPRINT",EDGE,{"derivedFrom":subQ0}),1.0]])]});}
            var Q8;
            {var subQ0=sQuery(id+"F0.wireOp",EDGE,"E62.filletArc");Q8=makeQuery(id+"F0.imprint","IMPRINT",FACE,{"disambiguationData":[TD([[makeQuery(id+"F0.imprint","IMPRINT",EDGE,{"derivedFrom":subQ0}),1.0]])]});}
            var Q9;
            {var subQ0=sQuery(id+"F0.wireOp",EDGE,"E44.filletArc");Q9=makeQuery(id+"F0.imprint","IMPRINT",FACE,{"disambiguationData":[TD([[makeQuery(id+"F0.imprint","IMPRINT",EDGE,{"derivedFrom":subQ0}),-1.0]])]});}
            var Q10;
            {var subQ0=sQuery(id+"F0.wireOp",EDGE,"E52.filletArc");Q10=makeQuery(id+"F0.imprint","IMPRINT",FACE,{"disambiguationData":[TD([[makeQuery(id+"F0.imprint","IMPRINT",EDGE,{"derivedFrom":subQ0}),1.0]])]});}
            var Q11;
            {var subQ0=sQuery(id+"F0.wireOp",EDGE,"E34.filletArc");Q11=makeQuery(id+"F0.imprint","IMPRINT",FACE,{"disambiguationData":[TD([[makeQuery(id+"F0.imprint","IMPRINT",EDGE,{"derivedFrom":subQ0}),1.0]])]});}
            var Q12;
            {var subQ30=sQuery(id+"F0.wireOp",EDGE,"E1.bottom");var subQ35=sQuery(id+"F0.wireOp",EDGE,"E1.left");var subQ56=makeQuery(id+"F0.imprint","INTERSECT",VERTEX,{"derivedFrom":[subQ30,subQ35]});Q12=makeQuery(id+"F0.imprint","IMPRINT",FACE,{"disambiguationData":[TD([[makeQuery(id+"F0.imprint","IMPRINT",EDGE,{"disambiguationData":[TD([[subQ56,-1.0]])],"derivedFrom":subQ30}),-1.0]])]});}
            var Q13;
            {var subQ0=sQuery(id+"F0.wireOp",EDGE,"E54");var subQ1=sQuery(id+"F0.wireOp",EDGE,"E1.left");var subQ2=makeQuery(id+"F0.imprint","INTERSECT",VERTEX,{"disambiguationData":[OD(0.0)],"derivedFrom":[subQ1,subQ0]});Q13=makeQuery(id+"F0.imprint","IMPRINT",FACE,{"disambiguationData":[TD([[makeQuery(id+"F0.imprint","IMPRINT",EDGE,{"disambiguationData":[TD([[subQ2,-1.0]])],"derivedFrom":subQ1}),-1.0]])]});}
            var Q14;
            {var subQ0=sQuery(id+"F0.wireOp",EDGE,"E12.left");var subQ1=sQuery(id+"F0.wireOp",EDGE,"E11");var subQ2=makeQuery(id+"F0.imprint","INTERSECT",VERTEX,{"derivedFrom":[subQ1,subQ0]});Q14=makeQuery(id+"F0.imprint","IMPRINT",FACE,{"disambiguationData":[TD([[makeQuery(id+"F0.imprint","IMPRINT",EDGE,{"disambiguationData":[TD([[subQ2,1.0]])],"derivedFrom":subQ1}),-1.0]])]});}
            var Q15;
            {var subQ0=sQuery(id+"F0.wireOp",EDGE,"E46.filletArc");Q15=makeQuery(id+"F0.imprint","IMPRINT",FACE,{"disambiguationData":[TD([[makeQuery(id+"F0.imprint","IMPRINT",EDGE,{"derivedFrom":subQ0}),-1.0]])]});}
            var Q16;
            {var subQ5=sQuery(id+"F0.wireOp",EDGE,"E42.filletArc");Q16=makeQuery(id+"F0.imprint","IMPRINT",FACE,{"disambiguationData":[TD([[makeQuery(id+"F0.imprint","IMPRINT",EDGE,{"derivedFrom":subQ5}),-1.0]])]});}
            var Q17;
            {var subQ0=sQuery(id+"F0.wireOp",EDGE,"E50.filletArc");Q17=makeQuery(id+"F0.imprint","IMPRINT",FACE,{"disambiguationData":[TD([[makeQuery(id+"F0.imprint","IMPRINT",EDGE,{"derivedFrom":subQ0}),1.0]])]});}
            var Q18;
            {var subQ0=sQuery(id+"F0.wireOp",EDGE,"E55.left");var subQ1=sQuery(id+"F0.wireOp",EDGE,"E54");var subQ2=makeQuery(id+"F0.imprint","INTERSECT",VERTEX,{"disambiguationData":[OD(0.0)],"derivedFrom":[subQ1,subQ0]});Q18=makeQuery(id+"F0.imprint","IMPRINT",FACE,{"disambiguationData":[TD([[makeQuery(id+"F0.imprint","IMPRINT",EDGE,{"disambiguationData":[TD([[subQ2,-1.0]])],"derivedFrom":subQ1}),1.0]])]});}
            var Q19;
            {var subQ0=sQuery(id+"F0.wireOp",EDGE,"E42.filletArc");Q19=makeQuery(id+"F0.imprint","IMPRINT",FACE,{"disambiguationData":[TD([[makeQuery(id+"F0.imprint","IMPRINT",EDGE,{"derivedFrom":subQ0}),1.0]])]});}
            var Q20;
            {var subQ6=sQuery(id+"F0.wireOp",EDGE,"E32.filletArc");Q20=makeQuery(id+"F0.imprint","IMPRINT",FACE,{"disambiguationData":[TD([[makeQuery(id+"F0.imprint","IMPRINT",EDGE,{"derivedFrom":subQ6}),-1.0]])]});}
            var Q21;
            {var subQ0=sQuery(id+"F0.wireOp",EDGE,"E16.left");var subQ1=sQuery(id+"F0.wireOp",EDGE,"E7");var subQ2=makeQuery(id+"F0.imprint","INTERSECT",VERTEX,{"derivedFrom":[subQ1,subQ0]});Q21=makeQuery(id+"F0.imprint","IMPRINT",FACE,{"disambiguationData":[TD([[makeQuery(id+"F0.imprint","IMPRINT",EDGE,{"disambiguationData":[TD([[subQ2,1.0]])],"derivedFrom":subQ1}),-1.0]])]});}
            var Q22;
            {var subQ0=sQuery(id+"F0.wireOp",EDGE,"E17.left");var subQ1=sQuery(id+"F0.wireOp",EDGE,"E8");var subQ2=makeQuery(id+"F0.imprint","INTERSECT",VERTEX,{"derivedFrom":[subQ1,subQ0]});Q22=makeQuery(id+"F0.imprint","IMPRINT",FACE,{"disambiguationData":[TD([[makeQuery(id+"F0.imprint","IMPRINT",EDGE,{"disambiguationData":[TD([[subQ2,1.0]])],"derivedFrom":subQ1}),-1.0]])]});}
            var Q23;
            {var subQ0=sQuery(id+"F0.wireOp",EDGE,"E30.filletArc");Q23=makeQuery(id+"F0.imprint","IMPRINT",FACE,{"disambiguationData":[TD([[makeQuery(id+"F0.imprint","IMPRINT",EDGE,{"derivedFrom":subQ0}),-1.0]])]});}
            var Q24;
            {var subQ5=sQuery(id+"F0.wireOp",EDGE,"E34.filletArc");Q24=makeQuery(id+"F0.imprint","IMPRINT",FACE,{"disambiguationData":[TD([[makeQuery(id+"F0.imprint","IMPRINT",EDGE,{"derivedFrom":subQ5}),-1.0]])]});}
            var Q25;
            {var subQ0=sQuery(id+"F0.wireOp",EDGE,"E30.filletArc");Q25=makeQuery(id+"F0.imprint","IMPRINT",FACE,{"disambiguationData":[TD([[makeQuery(id+"F0.imprint","IMPRINT",EDGE,{"derivedFrom":subQ0}),1.0]])]});}
            var Q26;
            {var subQ0=sQuery(id+"F0.wireOp",EDGE,"E35.filletArc");Q26=makeQuery(id+"F0.imprint","IMPRINT",FACE,{"disambiguationData":[TD([[makeQuery(id+"F0.imprint","IMPRINT",EDGE,{"derivedFrom":subQ0}),1.0]])]});}
            var Q27;
            {var subQ0=sQuery(id+"F0.wireOp",EDGE,"E35.filletArc");Q27=makeQuery(id+"F0.imprint","IMPRINT",FACE,{"disambiguationData":[TD([[makeQuery(id+"F0.imprint","IMPRINT",EDGE,{"derivedFrom":subQ0}),-1.0]])]});}
            var Q28;
            {var subQ6=sQuery(id+"F0.wireOp",EDGE,"E52.filletArc");Q28=makeQuery(id+"F0.imprint","IMPRINT",FACE,{"disambiguationData":[TD([[makeQuery(id+"F0.imprint","IMPRINT",EDGE,{"derivedFrom":subQ6}),-1.0]])]});}
            var Q29;
            {var subQ0=sQuery(id+"F0.wireOp",EDGE,"E44.filletArc");Q29=makeQuery(id+"F0.imprint","IMPRINT",FACE,{"disambiguationData":[TD([[makeQuery(id+"F0.imprint","IMPRINT",EDGE,{"derivedFrom":subQ0}),1.0]])]});}
            var Q30;
            {var subQ0=sQuery(id+"F0.wireOp",EDGE,"E40.filletArc");Q30=makeQuery(id+"F0.imprint","IMPRINT",FACE,{"disambiguationData":[TD([[makeQuery(id+"F0.imprint","IMPRINT",EDGE,{"derivedFrom":subQ0}),-1.0]])]});}
            var Q31;
            {var subQ6=sQuery(id+"F0.wireOp",EDGE,"E32.filletArc");Q31=makeQuery(id+"F0.imprint","IMPRINT",FACE,{"disambiguationData":[TD([[makeQuery(id+"F0.imprint","IMPRINT",EDGE,{"derivedFrom":subQ6}),1.0]])]});}
            var Q32;
            {var subQ4=sQuery(id+"F0.wireOp",EDGE,"E40.filletArc");Q32=makeQuery(id+"F0.imprint","IMPRINT",FACE,{"disambiguationData":[TD([[makeQuery(id+"F0.imprint","IMPRINT",EDGE,{"derivedFrom":subQ4}),1.0]])]});}
            var Q33;
            {var subQ0=sQuery(id+"F0.wireOp",EDGE,"E54");var subQ1=sQuery(id+"F0.wireOp",EDGE,"E1.left");var subQ2=makeQuery(id+"F0.imprint","INTERSECT",VERTEX,{"disambiguationData":[OD(0.0)],"derivedFrom":[subQ1,subQ0]});Q33=makeQuery(id+"F0.imprint","IMPRINT",FACE,{"disambiguationData":[TD([[makeQuery(id+"F0.imprint","IMPRINT",EDGE,{"disambiguationData":[TD([[subQ2,-1.0]])],"derivedFrom":subQ1}),1.0]])]});}
            var Q34;
            {var subQ0=sQuery(id+"F0.wireOp",EDGE,"E48.filletArc");Q34=makeQuery(id+"F0.imprint","IMPRINT",FACE,{"disambiguationData":[TD([[makeQuery(id+"F0.imprint","IMPRINT",EDGE,{"derivedFrom":subQ0}),-1.0]])]});}
            var Q35;
            {var subQ0=sQuery(id+"F0.wireOp",EDGE,"E61.filletArc");Q35=makeQuery(id+"F0.imprint","IMPRINT",FACE,{"disambiguationData":[TD([[makeQuery(id+"F0.imprint","IMPRINT",EDGE,{"derivedFrom":subQ0}),1.0]])]});}
            var Q36;
            Q36=makeQuery(id+"F0.imprint","IMPRINT",FACE,{"disambiguationData":[TD([[makeQuery(id+"F0.imprint","IMPRINT",EDGE,{"derivedFrom":sQuery(id+"F0.wireOp",EDGE,"E69")}),1.0]])]});
            var Q37;
            Q37=makeQuery(id+"F0.imprint","IMPRINT",FACE,{"disambiguationData":[TD([[makeQuery(id+"F0.imprint","IMPRINT",EDGE,{"derivedFrom":sQuery(id+"F0.wireOp",EDGE,"E74")}),1.0]])]});
            var Q38;
            Q38=makeQuery(id+"F0.imprint","IMPRINT",FACE,{"disambiguationData":[TD([[makeQuery(id+"F0.imprint","IMPRINT",EDGE,{"derivedFrom":sQuery(id+"F0.wireOp",EDGE,"E72")}),1.0]])]});
            var Q39;
            Q39=makeQuery(id+"F0.imprint","IMPRINT",FACE,{"disambiguationData":[TD([[makeQuery(id+"F0.imprint","IMPRINT",EDGE,{"derivedFrom":sQuery(id+"F0.wireOp",EDGE,"E79")}),1.0]])]});
            var Q40;
            Q40=makeQuery(id+"F0.imprint","IMPRINT",FACE,{"disambiguationData":[TD([[makeQuery(id+"F0.imprint","IMPRINT",EDGE,{"derivedFrom":sQuery(id+"F0.wireOp",EDGE,"E78")}),1.0]])]});
            var Q41;
            Q41=makeQuery(id+"F0.imprint","IMPRINT",FACE,{"disambiguationData":[TD([[makeQuery(id+"F0.imprint","IMPRINT",EDGE,{"derivedFrom":sQuery(id+"F0.wireOp",EDGE,"E77")}),1.0]])]});
            var Q42;
            Q42=makeQuery(id+"F0.imprint","IMPRINT",FACE,{"disambiguationData":[TD([[makeQuery(id+"F0.imprint","IMPRINT",EDGE,{"derivedFrom":sQuery(id+"F0.wireOp",EDGE,"E76")}),1.0]])]});
            var Q43;
            Q43=makeQuery(id+"F0.imprint","IMPRINT",FACE,{"disambiguationData":[TD([[makeQuery(id+"F0.imprint","IMPRINT",EDGE,{"derivedFrom":sQuery(id+"F0.wireOp",EDGE,"E75")}),1.0]])]});
            var Q44;
            Q44=makeQuery(id+"F0.imprint","IMPRINT",FACE,{"disambiguationData":[TD([[makeQuery(id+"F0.imprint","IMPRINT",EDGE,{"derivedFrom":sQuery(id+"F0.wireOp",EDGE,"E70")}),1.0]])]});
            var Q45;
            Q45=makeQuery(id+"F0.imprint","IMPRINT",FACE,{"disambiguationData":[TD([[makeQuery(id+"F0.imprint","IMPRINT",EDGE,{"derivedFrom":sQuery(id+"F0.wireOp",EDGE,"E73")}),1.0]])]});
            var Q46;
            Q46=makeQuery(id+"F0.imprint","IMPRINT",FACE,{"disambiguationData":[TD([[makeQuery(id+"F0.imprint","IMPRINT",EDGE,{"derivedFrom":sQuery(id+"F0.wireOp",EDGE,"E80")}),1.0]])]});
            var Q47;
            Q47=makeQuery(id+"F0.imprint","IMPRINT",FACE,{"disambiguationData":[TD([[makeQuery(id+"F0.imprint","IMPRINT",EDGE,{"derivedFrom":sQuery(id+"F0.wireOp",EDGE,"E71")}),1.0]])]});
            var Q48;
            {var subQ0=sQuery(id+"F0.wireOp",EDGE,"E63.filletArc");Q48=makeQuery(id+"F0.imprint","IMPRINT",FACE,{"disambiguationData":[TD([[makeQuery(id+"F0.imprint","IMPRINT",EDGE,{"derivedFrom":subQ0}),1.0]])]});}
            var Q49;
            {var subQ0=sQuery(id+"F0.wireOp",EDGE,"E64.filletArc");Q49=makeQuery(id+"F0.imprint","IMPRINT",FACE,{"disambiguationData":[TD([[makeQuery(id+"F0.imprint","IMPRINT",EDGE,{"derivedFrom":subQ0}),1.0]])]});}
            extrude(context, id + "F5", {"entities" : qUnion([Q0, Q1, Q2, Q3, Q4, Q5, Q6, Q7, Q8, Q9, Q10, Q11, Q12, Q13, Q14, Q15, Q16, Q17, Q18, Q19, Q20, Q21, Q22, Q23, Q24, Q25, Q26, Q27, Q28, Q29, Q30, Q31, Q32, Q33, Q34, Q35, Q36, Q37, Q38, Q39, Q40, Q41, Q42, Q43, Q44, Q45, Q46, Q47, Q48, Q49]), "operationType" : NewBodyOperationType.REMOVE, "depth" : 9.5 * mm, "offsetDistance" : 25 * mm});
        }
        {
            var Q0;
            {var subQ5=sQuery(id+"F0.wireOp",EDGE,"E55.bottom");Q0=makeQuery(id+"F0.imprint","IMPRINT",FACE,{"disambiguationData":[TD([[makeQuery(id+"F0.imprint","IMPRINT",EDGE,{"derivedFrom":subQ5}),-1.0]])]});}
            var Q1;
            {var subQ5=sQuery(id+"F0.wireOp",EDGE,"E55.right");Q1=makeQuery(id+"F0.imprint","IMPRINT",FACE,{"disambiguationData":[TD([[makeQuery(id+"F0.imprint","IMPRINT",EDGE,{"derivedFrom":subQ5}),-1.0]])]});}
            var Q2;
            {var subQ5=sQuery(id+"F0.wireOp",EDGE,"E55.top");Q2=makeQuery(id+"F0.imprint","IMPRINT",FACE,{"disambiguationData":[TD([[makeQuery(id+"F0.imprint","IMPRINT",EDGE,{"derivedFrom":subQ5}),1.0]])]});}
            var Q3;
            {var subQ0=sQuery(id+"F0.wireOp",EDGE,"E60");var subQ6=sQuery(id+"F0.wireOp",EDGE,"E1.left");var subQ7=makeQuery(id+"F0.imprint","INTERSECT",VERTEX,{"derivedFrom":[subQ6,subQ0]});Q3=makeQuery(id+"F0.imprint","IMPRINT",FACE,{"disambiguationData":[TD([[makeQuery(id+"F0.imprint","IMPRINT",EDGE,{"disambiguationData":[TD([[subQ7,1.0]])],"derivedFrom":subQ6}),-1.0]])]});}
            var Q4;
            {var subQ4=sQuery(id+"F0.wireOp",EDGE,"E56");Q4=makeQuery(id+"F0.imprint","IMPRINT",FACE,{"disambiguationData":[TD([[makeQuery(id+"F0.imprint","IMPRINT",EDGE,{"derivedFrom":subQ4}),-1.0]])]});}
            var Q5;
            {var subQ4=sQuery(id+"F0.wireOp",EDGE,"E57");var subQ6=sQuery(id+"F0.wireOp",EDGE,"E1.left");var subQ8=makeQuery(id+"F0.imprint","INTERSECT",VERTEX,{"derivedFrom":[subQ6,subQ4]});Q5=makeQuery(id+"F0.imprint","IMPRINT",FACE,{"disambiguationData":[TD([[makeQuery(id+"F0.imprint","IMPRINT",EDGE,{"disambiguationData":[TD([[subQ8,-1.0]])],"derivedFrom":subQ6}),-1.0]])]});}
            extrude(context, id + "F6", {"entities" : qUnion([Q0, Q1, Q2, Q3, Q4, Q5]), "operationType" : NewBodyOperationType.REMOVE, "depth" : 9 * mm, "offsetDistance" : 25 * mm});
        }
        {
            var Q0;
            {var subQ0=sQuery(id+"F0.wireOp",EDGE,"E17.left");var subQ1=sQuery(id+"F0.wireOp",EDGE,"E8");var subQ2=makeQuery(id+"F0.imprint","INTERSECT",VERTEX,{"derivedFrom":[subQ1,subQ0]});Q0=makeQuery(id+"F0.imprint","IMPRINT",FACE,{"disambiguationData":[TD([[makeQuery(id+"F0.imprint","IMPRINT",EDGE,{"disambiguationData":[TD([[subQ2,1.0]])],"derivedFrom":subQ1}),-1.0]])]});}
            var Q1;
            {var subQ0=sQuery(id+"F0.wireOp",EDGE,"E16.left");var subQ1=sQuery(id+"F0.wireOp",EDGE,"E7");var subQ2=makeQuery(id+"F0.imprint","INTERSECT",VERTEX,{"derivedFrom":[subQ1,subQ0]});Q1=makeQuery(id+"F0.imprint","IMPRINT",FACE,{"disambiguationData":[TD([[makeQuery(id+"F0.imprint","IMPRINT",EDGE,{"disambiguationData":[TD([[subQ2,1.0]])],"derivedFrom":subQ1}),-1.0]])]});}
            var Q2;
            {var subQ0=sQuery(id+"F0.wireOp",EDGE,"E15.left");var subQ1=sQuery(id+"F0.wireOp",EDGE,"E6");var subQ2=makeQuery(id+"F0.imprint","INTERSECT",VERTEX,{"derivedFrom":[subQ1,subQ0]});Q2=makeQuery(id+"F0.imprint","IMPRINT",FACE,{"disambiguationData":[TD([[makeQuery(id+"F0.imprint","IMPRINT",EDGE,{"disambiguationData":[TD([[subQ2,1.0]])],"derivedFrom":subQ1}),-1.0]])]});}
            var Q3;
            {var subQ0=sQuery(id+"F0.wireOp",EDGE,"E14.left");var subQ1=sQuery(id+"F0.wireOp",EDGE,"E9");var subQ2=makeQuery(id+"F0.imprint","INTERSECT",VERTEX,{"derivedFrom":[subQ1,subQ0]});Q3=makeQuery(id+"F0.imprint","IMPRINT",FACE,{"disambiguationData":[TD([[makeQuery(id+"F0.imprint","IMPRINT",EDGE,{"disambiguationData":[TD([[subQ2,1.0]])],"derivedFrom":subQ1}),-1.0]])]});}
            var Q4;
            {var subQ0=sQuery(id+"F0.wireOp",EDGE,"E13.left");var subQ1=sQuery(id+"F0.wireOp",EDGE,"E10");var subQ2=makeQuery(id+"F0.imprint","INTERSECT",VERTEX,{"derivedFrom":[subQ1,subQ0]});Q4=makeQuery(id+"F0.imprint","IMPRINT",FACE,{"disambiguationData":[TD([[makeQuery(id+"F0.imprint","IMPRINT",EDGE,{"disambiguationData":[TD([[subQ2,1.0]])],"derivedFrom":subQ1}),-1.0]])]});}
            var Q5;
            {var subQ0=sQuery(id+"F0.wireOp",EDGE,"E12.left");var subQ1=sQuery(id+"F0.wireOp",EDGE,"E11");var subQ2=makeQuery(id+"F0.imprint","INTERSECT",VERTEX,{"derivedFrom":[subQ1,subQ0]});Q5=makeQuery(id+"F0.imprint","IMPRINT",FACE,{"disambiguationData":[TD([[makeQuery(id+"F0.imprint","IMPRINT",EDGE,{"disambiguationData":[TD([[subQ2,1.0]])],"derivedFrom":subQ1}),-1.0]])]});}
            var Q6;
            {var subQ0=sQuery(id+"F0.wireOp",EDGE,"E46.filletArc");Q6=makeQuery(id+"F0.imprint","IMPRINT",FACE,{"disambiguationData":[TD([[makeQuery(id+"F0.imprint","IMPRINT",EDGE,{"derivedFrom":subQ0}),1.0]])]});}
            var Q7;
            {var subQ0=sQuery(id+"F0.wireOp",EDGE,"E44.filletArc");Q7=makeQuery(id+"F0.imprint","IMPRINT",FACE,{"disambiguationData":[TD([[makeQuery(id+"F0.imprint","IMPRINT",EDGE,{"derivedFrom":subQ0}),1.0]])]});}
            var Q8;
            {var subQ0=sQuery(id+"F0.wireOp",EDGE,"E42.filletArc");Q8=makeQuery(id+"F0.imprint","IMPRINT",FACE,{"disambiguationData":[TD([[makeQuery(id+"F0.imprint","IMPRINT",EDGE,{"derivedFrom":subQ0}),1.0]])]});}
            var Q9;
            {var subQ5=sQuery(id+"F0.wireOp",EDGE,"E38.filletArc");Q9=makeQuery(id+"F0.imprint","IMPRINT",FACE,{"disambiguationData":[TD([[makeQuery(id+"F0.imprint","IMPRINT",EDGE,{"derivedFrom":subQ5}),1.0]])]});}
            var Q10;
            {var subQ0=sQuery(id+"F0.wireOp",EDGE,"E34.filletArc");Q10=makeQuery(id+"F0.imprint","IMPRINT",FACE,{"disambiguationData":[TD([[makeQuery(id+"F0.imprint","IMPRINT",EDGE,{"derivedFrom":subQ0}),1.0]])]});}
            var Q11;
            {var subQ6=sQuery(id+"F0.wireOp",EDGE,"E32.filletArc");Q11=makeQuery(id+"F0.imprint","IMPRINT",FACE,{"disambiguationData":[TD([[makeQuery(id+"F0.imprint","IMPRINT",EDGE,{"derivedFrom":subQ6}),1.0]])]});}
            var Q12;
            {var subQ0=sQuery(id+"F0.wireOp",EDGE,"E30.filletArc");Q12=makeQuery(id+"F0.imprint","IMPRINT",FACE,{"disambiguationData":[TD([[makeQuery(id+"F0.imprint","IMPRINT",EDGE,{"derivedFrom":subQ0}),1.0]])]});}
            var Q13;
            {var subQ0=sQuery(id+"F0.wireOp",EDGE,"E35.filletArc");Q13=makeQuery(id+"F0.imprint","IMPRINT",FACE,{"disambiguationData":[TD([[makeQuery(id+"F0.imprint","IMPRINT",EDGE,{"derivedFrom":subQ0}),1.0]])]});}
            var Q14;
            {var subQ4=sQuery(id+"F0.wireOp",EDGE,"E40.filletArc");Q14=makeQuery(id+"F0.imprint","IMPRINT",FACE,{"disambiguationData":[TD([[makeQuery(id+"F0.imprint","IMPRINT",EDGE,{"derivedFrom":subQ4}),1.0]])]});}
            var Q15;
            {var subQ0=sQuery(id+"F0.wireOp",EDGE,"E52.filletArc");Q15=makeQuery(id+"F0.imprint","IMPRINT",FACE,{"disambiguationData":[TD([[makeQuery(id+"F0.imprint","IMPRINT",EDGE,{"derivedFrom":subQ0}),1.0]])]});}
            var Q16;
            {var subQ0=sQuery(id+"F0.wireOp",EDGE,"E50.filletArc");Q16=makeQuery(id+"F0.imprint","IMPRINT",FACE,{"disambiguationData":[TD([[makeQuery(id+"F0.imprint","IMPRINT",EDGE,{"derivedFrom":subQ0}),1.0]])]});}
            var Q17;
            {var subQ0=sQuery(id+"F0.wireOp",EDGE,"E48.filletArc");Q17=makeQuery(id+"F0.imprint","IMPRINT",FACE,{"disambiguationData":[TD([[makeQuery(id+"F0.imprint","IMPRINT",EDGE,{"derivedFrom":subQ0}),1.0]])]});}
            var Q18;
            Q18=makeQuery(id+"F0.imprint","IMPRINT",FACE,{"disambiguationData":[TD([[makeQuery(id+"F0.imprint","IMPRINT",EDGE,{"derivedFrom":sQuery(id+"F0.wireOp",EDGE,"E80")}),1.0]])]});
            var Q19;
            Q19=makeQuery(id+"F0.imprint","IMPRINT",FACE,{"disambiguationData":[TD([[makeQuery(id+"F0.imprint","IMPRINT",EDGE,{"derivedFrom":sQuery(id+"F0.wireOp",EDGE,"E69")}),1.0]])]});
            var Q20;
            Q20=makeQuery(id+"F0.imprint","IMPRINT",FACE,{"disambiguationData":[TD([[makeQuery(id+"F0.imprint","IMPRINT",EDGE,{"derivedFrom":sQuery(id+"F0.wireOp",EDGE,"E70")}),1.0]])]});
            var Q21;
            Q21=makeQuery(id+"F0.imprint","IMPRINT",FACE,{"disambiguationData":[TD([[makeQuery(id+"F0.imprint","IMPRINT",EDGE,{"derivedFrom":sQuery(id+"F0.wireOp",EDGE,"E71")}),1.0]])]});
            var Q22;
            Q22=makeQuery(id+"F0.imprint","IMPRINT",FACE,{"disambiguationData":[TD([[makeQuery(id+"F0.imprint","IMPRINT",EDGE,{"derivedFrom":sQuery(id+"F0.wireOp",EDGE,"E72")}),1.0]])]});
            var Q23;
            Q23=makeQuery(id+"F0.imprint","IMPRINT",FACE,{"disambiguationData":[TD([[makeQuery(id+"F0.imprint","IMPRINT",EDGE,{"derivedFrom":sQuery(id+"F0.wireOp",EDGE,"E73")}),1.0]])]});
            var Q24;
            Q24=makeQuery(id+"F0.imprint","IMPRINT",FACE,{"disambiguationData":[TD([[makeQuery(id+"F0.imprint","IMPRINT",EDGE,{"derivedFrom":sQuery(id+"F0.wireOp",EDGE,"E74")}),1.0]])]});
            var Q25;
            Q25=makeQuery(id+"F0.imprint","IMPRINT",FACE,{"disambiguationData":[TD([[makeQuery(id+"F0.imprint","IMPRINT",EDGE,{"derivedFrom":sQuery(id+"F0.wireOp",EDGE,"E75")}),1.0]])]});
            var Q26;
            Q26=makeQuery(id+"F0.imprint","IMPRINT",FACE,{"disambiguationData":[TD([[makeQuery(id+"F0.imprint","IMPRINT",EDGE,{"derivedFrom":sQuery(id+"F0.wireOp",EDGE,"E76")}),1.0]])]});
            var Q27;
            Q27=makeQuery(id+"F0.imprint","IMPRINT",FACE,{"disambiguationData":[TD([[makeQuery(id+"F0.imprint","IMPRINT",EDGE,{"derivedFrom":sQuery(id+"F0.wireOp",EDGE,"E77")}),1.0]])]});
            var Q28;
            Q28=makeQuery(id+"F0.imprint","IMPRINT",FACE,{"disambiguationData":[TD([[makeQuery(id+"F0.imprint","IMPRINT",EDGE,{"derivedFrom":sQuery(id+"F0.wireOp",EDGE,"E78")}),1.0]])]});
            var Q29;
            Q29=makeQuery(id+"F0.imprint","IMPRINT",FACE,{"disambiguationData":[TD([[makeQuery(id+"F0.imprint","IMPRINT",EDGE,{"derivedFrom":sQuery(id+"F0.wireOp",EDGE,"E79")}),1.0]])]});
            extrude(context, id + "F7", {"entities" : qUnion([Q0, Q1, Q2, Q3, Q4, Q5, Q6, Q7, Q8, Q9, Q10, Q11, Q12, Q13, Q14, Q15, Q16, Q17, Q18, Q19, Q20, Q21, Q22, Q23, Q24, Q25, Q26, Q27, Q28, Q29]), "operationType" : NewBodyOperationType.REMOVE, "endBound" : BoundingType.THROUGH_ALL, "depth" : 25 * mm, "offsetDistance" : 25 * mm});
        }
        {
            var Q0;
            Q0=qCreatedBy(makeId("Front.planeOp"),FACE);
            var sketch = newSketch(context, id + "F8", { "sketchPlane" : qUnion([Q0])});
            skLineSegment(sketch, "E91.bottom", {"start": v(37.5, -12.5) * mm, "end": v(-37.5, -12.5) * mm});
            skLineSegment(sketch, "E91.top", {"start": v(37.5, 12.5) * mm, "end": v(-37.5, 12.5) * mm});
            skLineSegment(sketch, "E91.left", {"start": v(37.5, -12.5) * mm, "end": v(37.5, 12.5) * mm});
            skLineSegment(sketch, "E91.right", {"start": v(-37.5, -12.5) * mm, "end": v(-37.5, 12.5) * mm});
            skPoint(sketch, "E91.middle", {"position": v(0, 0) * mm});
            skCircle(sketch, "E92", {"center": v(24.75, -9) * mm, "radius": 0.38 * mm});
            skCircle(sketch, "E93.1.0.0", {"center": v(15.75, -9) * mm, "radius": 0.38 * mm});
            skLineSegment(sketch, "E93.direction1", {"start": v(24.75, -9) * mm, "end": v(15.75, -9) * mm, "construction": true});
            skCircle(sketch, "E94.0.2.0", {"center": v(6.75, -9) * mm, "radius": 0.38 * mm});
            skCircle(sketch, "E95.MirrorC", {"center": v(15.75, 9) * mm, "radius": 0.38 * mm});
            skCircle(sketch, "E96.MirrorC", {"center": v(24.75, 9) * mm, "radius": 0.38 * mm});
            skCircle(sketch, "E97.MirrorC", {"center": v(6.75, 9) * mm, "radius": 0.38 * mm});
            skCircle(sketch, "E98.MirrorC", {"center": v(-6.75, -9) * mm, "radius": 0.38 * mm});
            skCircle(sketch, "E99.MirrorC", {"center": v(-6.75, 9) * mm, "radius": 0.38 * mm});
            skCircle(sketch, "E100.MirrorC", {"center": v(-15.75, 9) * mm, "radius": 0.38 * mm});
            skCircle(sketch, "E101.MirrorC", {"center": v(-24.75, -9) * mm, "radius": 0.38 * mm});
            skCircle(sketch, "E102.MirrorC", {"center": v(-15.75, -9) * mm, "radius": 0.38 * mm});
            skCircle(sketch, "E103.MirrorC", {"center": v(-24.75, 9) * mm, "radius": 0.38 * mm});
            skEllipse(sketch, "E104", {"center": v(24.75, -8.22) * mm, "majorRadius": 1 * mm, "minorRadius": 0.5 * mm, "majorAxis": v(0, -1)});
            skLineSegment(sketch, "E105.bottom", {"start": v(25.25, -8.23) * mm, "end": v(24.25, -8.23) * mm});
            skLineSegment(sketch, "E105.top", {"start": v(25.25, 8.23) * mm, "end": v(24.25, 8.23) * mm});
            skLineSegment(sketch, "E105.left", {"start": v(25.25, -8.22) * mm, "end": v(25.25, 8.22) * mm});
            skLineSegment(sketch, "E105.right", {"start": v(24.25, -8.22) * mm, "end": v(24.25, 8.22) * mm});
            skEllipse(sketch, "E106.MirrorC", {"center": v(24.75, 8.23) * mm, "majorRadius": 1 * mm, "minorRadius": 0.5 * mm, "majorAxis": v(0, 1)});
            skEllipse(sketch, "E107.MirrorC", {"center": v(24.75, 8.23) * mm, "majorRadius": 1 * mm, "minorRadius": 0.5 * mm, "majorAxis": v(0, 1)});
            skLineSegment(sketch, "E108.1.0.0", {"start": v(15.25, -8.23) * mm, "end": v(15.25, 8.22) * mm});
            skLineSegment(sketch, "E108.1.0.1", {"start": v(16.25, -8.23) * mm, "end": v(16.25, 8.22) * mm});
            skEllipse(sketch, "E108.1.0.2", {"center": v(15.75, 8.22) * mm, "majorRadius": 1 * mm, "minorRadius": 0.5 * mm, "majorAxis": v(0, 1)});
            skLineSegment(sketch, "E108.1.0.3", {"start": v(16.25, 8.22) * mm, "end": v(15.25, 8.22) * mm});
            skLineSegment(sketch, "E108.1.0.4", {"start": v(16.25, -8.23) * mm, "end": v(15.25, -8.23) * mm});
            skEllipse(sketch, "E108.1.0.5", {"center": v(15.75, -8.23) * mm, "majorRadius": 1 * mm, "minorRadius": 0.5 * mm, "majorAxis": v(0, -1)});
            skLineSegment(sketch, "E108.2.0.0", {"start": v(6.25, -8.23) * mm, "end": v(6.25, 8.22) * mm});
            skLineSegment(sketch, "E108.2.0.1", {"start": v(7.25, -8.23) * mm, "end": v(7.25, 8.22) * mm});
            skEllipse(sketch, "E108.2.0.2", {"center": v(6.75, 8.22) * mm, "majorRadius": 1 * mm, "minorRadius": 0.5 * mm, "majorAxis": v(0, 1)});
            skLineSegment(sketch, "E108.2.0.3", {"start": v(7.25, 8.22) * mm, "end": v(6.25, 8.22) * mm});
            skLineSegment(sketch, "E108.2.0.4", {"start": v(7.25, -8.23) * mm, "end": v(6.25, -8.23) * mm});
            skEllipse(sketch, "E108.2.0.5", {"center": v(6.75, -8.23) * mm, "majorRadius": 1 * mm, "minorRadius": 0.5 * mm, "majorAxis": v(0, -1)});
            skLineSegment(sketch, "E108.direction1", {"start": v(24.25, -8.23) * mm, "end": v(15.25, -8.23) * mm, "construction": true});
            skLineSegment(sketch, "E109.MirrorCS", {"start": v(-24.25, -8.22) * mm, "end": v(-24.25, 8.22) * mm});
            skLineSegment(sketch, "E110.MirrorCS", {"start": v(-25.25, -8.22) * mm, "end": v(-25.25, 8.22) * mm});
            skEllipse(sketch, "E111.MirrorC", {"center": v(-24.75, 8.23) * mm, "majorRadius": 1 * mm, "minorRadius": 0.5 * mm, "majorAxis": v(0, 1)});
            skEllipse(sketch, "E112.MirrorC", {"center": v(-24.75, -8.23) * mm, "majorRadius": 1 * mm, "minorRadius": 0.5 * mm, "majorAxis": v(0, -1)});
            skLineSegment(sketch, "E113.MirrorCS", {"start": v(-16.25, -8.23) * mm, "end": v(-16.25, 8.22) * mm});
            skLineSegment(sketch, "E114.MirrorCS", {"start": v(-15.25, -8.23) * mm, "end": v(-15.25, 8.22) * mm});
            skEllipse(sketch, "E115.MirrorC", {"center": v(-15.75, -8.23) * mm, "majorRadius": 1 * mm, "minorRadius": 0.5 * mm, "majorAxis": v(0, -1)});
            skEllipse(sketch, "E116.MirrorC", {"center": v(-15.75, 8.22) * mm, "majorRadius": 1 * mm, "minorRadius": 0.5 * mm, "majorAxis": v(0, 1)});
            skLineSegment(sketch, "E117.MirrorCS", {"start": v(-7.25, -8.23) * mm, "end": v(-7.25, 8.22) * mm});
            skEllipse(sketch, "E118.MirrorC", {"center": v(-6.75, 8.22) * mm, "majorRadius": 1 * mm, "minorRadius": 0.5 * mm, "majorAxis": v(0, 1)});
            skLineSegment(sketch, "E119.MirrorCS", {"start": v(-6.25, -8.23) * mm, "end": v(-6.25, 8.22) * mm});
            skEllipse(sketch, "E120.MirrorC", {"center": v(-6.75, -8.23) * mm, "majorRadius": 1 * mm, "minorRadius": 0.5 * mm, "majorAxis": v(0, -1)});
            skLineSegment(sketch, "E121.bottom", {"start": v(-30, 12.5) * mm, "end": v(30, 12.5) * mm});
            skLineSegment(sketch, "E121.top", {"start": v(-30, -12.5) * mm, "end": v(30, -12.5) * mm});
            skLineSegment(sketch, "E121.left", {"start": v(-30, 12.5) * mm, "end": v(-30, -12.5) * mm});
            skLineSegment(sketch, "E121.right", {"start": v(30, 12.5) * mm, "end": v(30, -12.5) * mm});
            skSolve(sketch);
        }
        {
            var Q0;
            Q0=makeQuery(id+"F8.imprint","IMPRINT",FACE,{"disambiguationData":[TD([[makeQuery(id+"F8.imprint","IMPRINT",EDGE,{"derivedFrom":sQuery(id+"F8.wireOp",EDGE,"E91.bottom")}),-1.0]])]});
            var Q1;
            {var subQ15=sQuery(id+"F8.wireOp",EDGE,"E105.left");Q1=makeQuery(id+"F8.imprint","IMPRINT",FACE,{"disambiguationData":[TD([[makeQuery(id+"F8.imprint","IMPRINT",EDGE,{"derivedFrom":subQ15}),-1.0]])]});}
            var Q2;
            {var subQ0=sQuery(id+"F8.wireOp",EDGE,"E109.MirrorCS");Q2=makeQuery(id+"F8.imprint","IMPRINT",FACE,{"disambiguationData":[TD([[makeQuery(id+"F8.imprint","IMPRINT",EDGE,{"derivedFrom":subQ0}),1.0]])]});}
            var Q3;
            {var subQ0=sQuery(id+"F8.wireOp",EDGE,"E113.MirrorCS");Q3=makeQuery(id+"F8.imprint","IMPRINT",FACE,{"disambiguationData":[TD([[makeQuery(id+"F8.imprint","IMPRINT",EDGE,{"derivedFrom":subQ0}),-1.0]])]});}
            var Q4;
            Q4=makeQuery(id+"F8.imprint","IMPRINT",FACE,{"disambiguationData":[TD([[makeQuery(id+"F8.imprint","IMPRINT",EDGE,{"derivedFrom":sQuery(id+"F8.wireOp",EDGE,"E103.MirrorC")}),-1.0]])]});
            var Q5;
            {var subQ0=sQuery(id+"F8.wireOp",EDGE,"E117.MirrorCS");Q5=makeQuery(id+"F8.imprint","IMPRINT",FACE,{"disambiguationData":[TD([[makeQuery(id+"F8.imprint","IMPRINT",EDGE,{"derivedFrom":subQ0}),-1.0]])]});}
            var Q6;
            Q6=makeQuery(id+"F8.imprint","IMPRINT",FACE,{"disambiguationData":[TD([[makeQuery(id+"F8.imprint","IMPRINT",EDGE,{"derivedFrom":sQuery(id+"F8.wireOp",EDGE,"E100.MirrorC")}),-1.0]])]});
            var Q7;
            Q7=makeQuery(id+"F8.imprint","IMPRINT",FACE,{"disambiguationData":[TD([[makeQuery(id+"F8.imprint","IMPRINT",EDGE,{"derivedFrom":sQuery(id+"F8.wireOp",EDGE,"E102.MirrorC")}),1.0]])]});
            var Q8;
            Q8=makeQuery(id+"F8.imprint","IMPRINT",FACE,{"disambiguationData":[TD([[makeQuery(id+"F8.imprint","IMPRINT",EDGE,{"derivedFrom":sQuery(id+"F8.wireOp",EDGE,"E98.MirrorC")}),1.0]])]});
            var Q9;
            Q9=makeQuery(id+"F8.imprint","IMPRINT",FACE,{"disambiguationData":[TD([[makeQuery(id+"F8.imprint","IMPRINT",EDGE,{"derivedFrom":sQuery(id+"F8.wireOp",EDGE,"E99.MirrorC")}),-1.0]])]});
            var Q10;
            {var subQ0=sQuery(id+"F8.wireOp",EDGE,"E108.2.0.0");Q10=makeQuery(id+"F8.imprint","IMPRINT",FACE,{"disambiguationData":[TD([[makeQuery(id+"F8.imprint","IMPRINT",EDGE,{"derivedFrom":subQ0}),-1.0]])]});}
            var Q11;
            {var subQ0=sQuery(id+"F8.wireOp",EDGE,"E108.2.0.4");Q11=makeQuery(id+"F8.imprint","IMPRINT",FACE,{"disambiguationData":[TD([[makeQuery(id+"F8.imprint","IMPRINT",EDGE,{"derivedFrom":subQ0}),-1.0]])]});}
            var Q12;
            {var subQ0=sQuery(id+"F8.wireOp",EDGE,"E108.1.0.4");Q12=makeQuery(id+"F8.imprint","IMPRINT",FACE,{"disambiguationData":[TD([[makeQuery(id+"F8.imprint","IMPRINT",EDGE,{"derivedFrom":subQ0}),-1.0]])]});}
            var Q13;
            {var subQ0=sQuery(id+"F8.wireOp",EDGE,"E108.1.0.0");Q13=makeQuery(id+"F8.imprint","IMPRINT",FACE,{"disambiguationData":[TD([[makeQuery(id+"F8.imprint","IMPRINT",EDGE,{"derivedFrom":subQ0}),-1.0]])]});}
            var Q14;
            Q14=makeQuery(id+"F8.imprint","IMPRINT",FACE,{"disambiguationData":[TD([[makeQuery(id+"F8.imprint","IMPRINT",EDGE,{"derivedFrom":sQuery(id+"F8.wireOp",EDGE,"E97.MirrorC")}),1.0]])]});
            var Q15;
            {var subQ0=sQuery(id+"F8.wireOp",EDGE,"E108.2.0.3");Q15=makeQuery(id+"F8.imprint","IMPRINT",FACE,{"disambiguationData":[TD([[makeQuery(id+"F8.imprint","IMPRINT",EDGE,{"derivedFrom":subQ0}),1.0]])]});}
            var Q16;
            Q16=makeQuery(id+"F8.imprint","IMPRINT",FACE,{"disambiguationData":[TD([[makeQuery(id+"F8.imprint","IMPRINT",EDGE,{"derivedFrom":sQuery(id+"F8.wireOp",EDGE,"E94.0.2.0")}),-1.0]])]});
            var Q17;
            Q17=makeQuery(id+"F8.imprint","IMPRINT",FACE,{"disambiguationData":[TD([[makeQuery(id+"F8.imprint","IMPRINT",EDGE,{"derivedFrom":sQuery(id+"F8.wireOp",EDGE,"E93.1.0.0")}),-1.0]])]});
            var Q18;
            {var subQ0=sQuery(id+"F8.wireOp",EDGE,"E108.1.0.3");Q18=makeQuery(id+"F8.imprint","IMPRINT",FACE,{"disambiguationData":[TD([[makeQuery(id+"F8.imprint","IMPRINT",EDGE,{"derivedFrom":subQ0}),1.0]])]});}
            var Q19;
            Q19=makeQuery(id+"F8.imprint","IMPRINT",FACE,{"disambiguationData":[TD([[makeQuery(id+"F8.imprint","IMPRINT",EDGE,{"derivedFrom":sQuery(id+"F8.wireOp",EDGE,"E95.MirrorC")}),1.0]])]});
            var Q20;
            Q20=makeQuery(id+"F8.imprint","IMPRINT",FACE,{"disambiguationData":[TD([[makeQuery(id+"F8.imprint","IMPRINT",EDGE,{"derivedFrom":sQuery(id+"F8.wireOp",EDGE,"E101.MirrorC")}),1.0]])]});
            var Q21;
            Q21=makeQuery(id+"F8.imprint","IMPRINT",FACE,{"disambiguationData":[TD([[makeQuery(id+"F8.imprint","IMPRINT",EDGE,{"derivedFrom":sQuery(id+"F8.wireOp",EDGE,"E96.MirrorC")}),1.0]])]});
            var Q22;
            {var subQ0=sQuery(id+"F8.wireOp",EDGE,"E105.top");Q22=makeQuery(id+"F8.imprint","IMPRINT",FACE,{"disambiguationData":[TD([[makeQuery(id+"F8.imprint","IMPRINT",EDGE,{"derivedFrom":subQ0}),1.0]])]});}
            var Q23;
            {var subQ0=sQuery(id+"F8.wireOp",EDGE,"E105.left");Q23=makeQuery(id+"F8.imprint","IMPRINT",FACE,{"disambiguationData":[TD([[makeQuery(id+"F8.imprint","IMPRINT",EDGE,{"derivedFrom":subQ0}),1.0]])]});}
            var Q24;
            {var subQ0=sQuery(id+"F8.wireOp",EDGE,"E105.bottom");Q24=makeQuery(id+"F8.imprint","IMPRINT",FACE,{"disambiguationData":[TD([[makeQuery(id+"F8.imprint","IMPRINT",EDGE,{"derivedFrom":subQ0}),-1.0]])]});}
            var Q25;
            Q25=makeQuery(id+"F8.imprint","IMPRINT",FACE,{"disambiguationData":[TD([[makeQuery(id+"F8.imprint","IMPRINT",EDGE,{"derivedFrom":sQuery(id+"F8.wireOp",EDGE,"E92")}),-1.0]])]});
            extrude(context, id + "F9", {"entities" : qUnion([Q0, Q1, Q2, Q3, Q4, Q5, Q6, Q7, Q8, Q9, Q10, Q11, Q12, Q13, Q14, Q15, Q16, Q17, Q18, Q19, Q20, Q21, Q22, Q23, Q24, Q25]), "depth" : 1 * mm, "offsetDistance" : 25 * mm});
        }
        {
            var Q0;
            {var subQ15=sQuery(id+"F8.wireOp",EDGE,"E105.left");Q0=makeQuery(id+"F8.imprint","IMPRINT",FACE,{"disambiguationData":[TD([[makeQuery(id+"F8.imprint","IMPRINT",EDGE,{"derivedFrom":subQ15}),-1.0]])]});}
            var Q1;
            {var subQ0=sQuery(id+"F8.wireOp",EDGE,"E91.right");Q1=makeQuery(id+"F8.imprint","IMPRINT",FACE,{"disambiguationData":[TD([[makeQuery(id+"F8.imprint","IMPRINT",EDGE,{"derivedFrom":subQ0}),-1.0]])]});}
            var Q2;
            {var subQ0=sQuery(id+"F8.wireOp",EDGE,"E91.left");Q2=makeQuery(id+"F8.imprint","IMPRINT",FACE,{"disambiguationData":[TD([[makeQuery(id+"F8.imprint","IMPRINT",EDGE,{"derivedFrom":subQ0}),1.0]])]});}
            extrude(context, id + "F10", {"entities" : qUnion([Q0, Q1, Q2]), "oppositeDirection" : true, "depth" : .150 * mm, "offsetDistance" : 25 * mm});
        }
        {
            var Q0;
            {var subQ15=sQuery(id+"F8.wireOp",EDGE,"E105.left");Q0=makeQuery(id+"F8.imprint","IMPRINT",FACE,{"disambiguationData":[TD([[makeQuery(id+"F8.imprint","IMPRINT",EDGE,{"derivedFrom":subQ15}),-1.0]])]});}
            var Q1;
            {var subQ0=sQuery(id+"F8.wireOp",EDGE,"E117.MirrorCS");Q1=makeQuery(id+"F8.imprint","IMPRINT",FACE,{"disambiguationData":[TD([[makeQuery(id+"F8.imprint","IMPRINT",EDGE,{"derivedFrom":subQ0}),-1.0]])]});}
            var Q2;
            Q2=makeQuery(id+"F8.imprint","IMPRINT",FACE,{"disambiguationData":[TD([[makeQuery(id+"F8.imprint","IMPRINT",EDGE,{"derivedFrom":sQuery(id+"F8.wireOp",EDGE,"E102.MirrorC")}),1.0]])]});
            var Q3;
            {var subQ0=sQuery(id+"F8.wireOp",EDGE,"E108.2.0.4");Q3=makeQuery(id+"F8.imprint","IMPRINT",FACE,{"disambiguationData":[TD([[makeQuery(id+"F8.imprint","IMPRINT",EDGE,{"derivedFrom":subQ0}),-1.0]])]});}
            var Q4;
            {var subQ0=sQuery(id+"F8.wireOp",EDGE,"E109.MirrorCS");Q4=makeQuery(id+"F8.imprint","IMPRINT",FACE,{"disambiguationData":[TD([[makeQuery(id+"F8.imprint","IMPRINT",EDGE,{"derivedFrom":subQ0}),1.0]])]});}
            var Q5;
            {var subQ0=sQuery(id+"F8.wireOp",EDGE,"E105.top");Q5=makeQuery(id+"F8.imprint","IMPRINT",FACE,{"disambiguationData":[TD([[makeQuery(id+"F8.imprint","IMPRINT",EDGE,{"derivedFrom":subQ0}),1.0]])]});}
            var Q6;
            {var subQ0=sQuery(id+"F8.wireOp",EDGE,"E108.2.0.3");Q6=makeQuery(id+"F8.imprint","IMPRINT",FACE,{"disambiguationData":[TD([[makeQuery(id+"F8.imprint","IMPRINT",EDGE,{"derivedFrom":subQ0}),1.0]])]});}
            var Q7;
            {var subQ0=sQuery(id+"F8.wireOp",EDGE,"E113.MirrorCS");Q7=makeQuery(id+"F8.imprint","IMPRINT",FACE,{"disambiguationData":[TD([[makeQuery(id+"F8.imprint","IMPRINT",EDGE,{"derivedFrom":subQ0}),-1.0]])]});}
            var Q8;
            {var subQ0=sQuery(id+"F8.wireOp",EDGE,"E108.2.0.0");Q8=makeQuery(id+"F8.imprint","IMPRINT",FACE,{"disambiguationData":[TD([[makeQuery(id+"F8.imprint","IMPRINT",EDGE,{"derivedFrom":subQ0}),-1.0]])]});}
            var Q9;
            {var subQ0=sQuery(id+"F8.wireOp",EDGE,"E108.1.0.4");Q9=makeQuery(id+"F8.imprint","IMPRINT",FACE,{"disambiguationData":[TD([[makeQuery(id+"F8.imprint","IMPRINT",EDGE,{"derivedFrom":subQ0}),-1.0]])]});}
            var Q10;
            Q10=makeQuery(id+"F8.imprint","IMPRINT",FACE,{"disambiguationData":[TD([[makeQuery(id+"F8.imprint","IMPRINT",EDGE,{"derivedFrom":sQuery(id+"F8.wireOp",EDGE,"E103.MirrorC")}),-1.0]])]});
            var Q11;
            {var subQ0=sQuery(id+"F8.wireOp",EDGE,"E105.bottom");Q11=makeQuery(id+"F8.imprint","IMPRINT",FACE,{"disambiguationData":[TD([[makeQuery(id+"F8.imprint","IMPRINT",EDGE,{"derivedFrom":subQ0}),-1.0]])]});}
            var Q12;
            Q12=makeQuery(id+"F8.imprint","IMPRINT",FACE,{"disambiguationData":[TD([[makeQuery(id+"F8.imprint","IMPRINT",EDGE,{"derivedFrom":sQuery(id+"F8.wireOp",EDGE,"E98.MirrorC")}),1.0]])]});
            var Q13;
            Q13=makeQuery(id+"F8.imprint","IMPRINT",FACE,{"disambiguationData":[TD([[makeQuery(id+"F8.imprint","IMPRINT",EDGE,{"derivedFrom":sQuery(id+"F8.wireOp",EDGE,"E99.MirrorC")}),-1.0]])]});
            var Q14;
            {var subQ0=sQuery(id+"F8.wireOp",EDGE,"E105.left");Q14=makeQuery(id+"F8.imprint","IMPRINT",FACE,{"disambiguationData":[TD([[makeQuery(id+"F8.imprint","IMPRINT",EDGE,{"derivedFrom":subQ0}),1.0]])]});}
            var Q15;
            {var subQ0=sQuery(id+"F8.wireOp",EDGE,"E108.1.0.3");Q15=makeQuery(id+"F8.imprint","IMPRINT",FACE,{"disambiguationData":[TD([[makeQuery(id+"F8.imprint","IMPRINT",EDGE,{"derivedFrom":subQ0}),1.0]])]});}
            var Q16;
            {var subQ0=sQuery(id+"F8.wireOp",EDGE,"E108.1.0.0");Q16=makeQuery(id+"F8.imprint","IMPRINT",FACE,{"disambiguationData":[TD([[makeQuery(id+"F8.imprint","IMPRINT",EDGE,{"derivedFrom":subQ0}),-1.0]])]});}
            var Q17;
            Q17=makeQuery(id+"F8.imprint","IMPRINT",FACE,{"disambiguationData":[TD([[makeQuery(id+"F8.imprint","IMPRINT",EDGE,{"derivedFrom":sQuery(id+"F8.wireOp",EDGE,"E100.MirrorC")}),-1.0]])]});
            var Q18;
            Q18=makeQuery(id+"F8.imprint","IMPRINT",FACE,{"disambiguationData":[TD([[makeQuery(id+"F8.imprint","IMPRINT",EDGE,{"derivedFrom":sQuery(id+"F8.wireOp",EDGE,"E101.MirrorC")}),1.0]])]});
            var Q19;
            Q19=makeQuery(id+"F8.imprint","IMPRINT",FACE,{"disambiguationData":[TD([[makeQuery(id+"F8.imprint","IMPRINT",EDGE,{"derivedFrom":sQuery(id+"F8.wireOp",EDGE,"E96.MirrorC")}),-1.0]])]});
            var Q20;
            Q20=makeQuery(id+"F8.imprint","IMPRINT",FACE,{"disambiguationData":[TD([[makeQuery(id+"F8.imprint","IMPRINT",EDGE,{"derivedFrom":sQuery(id+"F8.wireOp",EDGE,"E103.MirrorC")}),1.0]])]});
            var Q21;
            Q21=makeQuery(id+"F8.imprint","IMPRINT",FACE,{"disambiguationData":[TD([[makeQuery(id+"F8.imprint","IMPRINT",EDGE,{"derivedFrom":sQuery(id+"F8.wireOp",EDGE,"E99.MirrorC")}),1.0]])]});
            var Q22;
            Q22=makeQuery(id+"F8.imprint","IMPRINT",FACE,{"disambiguationData":[TD([[makeQuery(id+"F8.imprint","IMPRINT",EDGE,{"derivedFrom":sQuery(id+"F8.wireOp",EDGE,"E95.MirrorC")}),1.0]])]});
            var Q23;
            Q23=makeQuery(id+"F8.imprint","IMPRINT",FACE,{"disambiguationData":[TD([[makeQuery(id+"F8.imprint","IMPRINT",EDGE,{"derivedFrom":sQuery(id+"F8.wireOp",EDGE,"E100.MirrorC")}),1.0]])]});
            var Q24;
            Q24=makeQuery(id+"F8.imprint","IMPRINT",FACE,{"disambiguationData":[TD([[makeQuery(id+"F8.imprint","IMPRINT",EDGE,{"derivedFrom":sQuery(id+"F8.wireOp",EDGE,"E97.MirrorC")}),-1.0]])]});
            var Q25;
            Q25=makeQuery(id+"F8.imprint","IMPRINT",FACE,{"disambiguationData":[TD([[makeQuery(id+"F8.imprint","IMPRINT",EDGE,{"derivedFrom":sQuery(id+"F8.wireOp",EDGE,"E95.MirrorC")}),-1.0]])]});
            var Q26;
            Q26=makeQuery(id+"F8.imprint","IMPRINT",FACE,{"disambiguationData":[TD([[makeQuery(id+"F8.imprint","IMPRINT",EDGE,{"derivedFrom":sQuery(id+"F8.wireOp",EDGE,"E97.MirrorC")}),1.0]])]});
            var Q27;
            Q27=makeQuery(id+"F8.imprint","IMPRINT",FACE,{"disambiguationData":[TD([[makeQuery(id+"F8.imprint","IMPRINT",EDGE,{"derivedFrom":sQuery(id+"F8.wireOp",EDGE,"E94.0.2.0")}),-1.0]])]});
            var Q28;
            Q28=makeQuery(id+"F8.imprint","IMPRINT",FACE,{"disambiguationData":[TD([[makeQuery(id+"F8.imprint","IMPRINT",EDGE,{"derivedFrom":sQuery(id+"F8.wireOp",EDGE,"E94.0.2.0")}),1.0]])]});
            var Q29;
            Q29=makeQuery(id+"F8.imprint","IMPRINT",FACE,{"disambiguationData":[TD([[makeQuery(id+"F8.imprint","IMPRINT",EDGE,{"derivedFrom":sQuery(id+"F8.wireOp",EDGE,"E98.MirrorC")}),-1.0]])]});
            var Q30;
            Q30=makeQuery(id+"F8.imprint","IMPRINT",FACE,{"disambiguationData":[TD([[makeQuery(id+"F8.imprint","IMPRINT",EDGE,{"derivedFrom":sQuery(id+"F8.wireOp",EDGE,"E92")}),-1.0]])]});
            var Q31;
            Q31=makeQuery(id+"F8.imprint","IMPRINT",FACE,{"disambiguationData":[TD([[makeQuery(id+"F8.imprint","IMPRINT",EDGE,{"derivedFrom":sQuery(id+"F8.wireOp",EDGE,"E93.1.0.0")}),-1.0]])]});
            var Q32;
            Q32=makeQuery(id+"F8.imprint","IMPRINT",FACE,{"disambiguationData":[TD([[makeQuery(id+"F8.imprint","IMPRINT",EDGE,{"derivedFrom":sQuery(id+"F8.wireOp",EDGE,"E96.MirrorC")}),1.0]])]});
            var Q33;
            Q33=makeQuery(id+"F8.imprint","IMPRINT",FACE,{"disambiguationData":[TD([[makeQuery(id+"F8.imprint","IMPRINT",EDGE,{"derivedFrom":sQuery(id+"F8.wireOp",EDGE,"E102.MirrorC")}),-1.0]])]});
            var Q34;
            Q34=makeQuery(id+"F8.imprint","IMPRINT",FACE,{"disambiguationData":[TD([[makeQuery(id+"F8.imprint","IMPRINT",EDGE,{"derivedFrom":sQuery(id+"F8.wireOp",EDGE,"E101.MirrorC")}),-1.0]])]});
            var Q35;
            Q35=makeQuery(id+"F8.imprint","IMPRINT",FACE,{"disambiguationData":[TD([[makeQuery(id+"F8.imprint","IMPRINT",EDGE,{"derivedFrom":sQuery(id+"F8.wireOp",EDGE,"E92")}),1.0]])]});
            var Q36;
            Q36=makeQuery(id+"F8.imprint","IMPRINT",FACE,{"disambiguationData":[TD([[makeQuery(id+"F8.imprint","IMPRINT",EDGE,{"derivedFrom":sQuery(id+"F8.wireOp",EDGE,"E93.1.0.0")}),1.0]])]});
            var Q37;
            {var subQ0=sQuery(id+"F8.wireOp",EDGE,"E91.right");Q37=makeQuery(id+"F8.imprint","IMPRINT",FACE,{"disambiguationData":[TD([[makeQuery(id+"F8.imprint","IMPRINT",EDGE,{"derivedFrom":subQ0}),-1.0]])]});}
            var Q38;
            {var subQ0=sQuery(id+"F8.wireOp",EDGE,"E91.left");Q38=makeQuery(id+"F8.imprint","IMPRINT",FACE,{"disambiguationData":[TD([[makeQuery(id+"F8.imprint","IMPRINT",EDGE,{"derivedFrom":subQ0}),1.0]])]});}
            extrude(context, id + "F11", {"entities" : qUnion([Q0, Q1, Q2, Q3, Q4, Q5, Q6, Q7, Q8, Q9, Q10, Q11, Q12, Q13, Q14, Q15, Q16, Q17, Q18, Q19, Q20, Q21, Q22, Q23, Q24, Q25, Q26, Q27, Q28, Q29, Q30, Q31, Q32, Q33, Q34, Q35, Q36, Q37, Q38]), "oppositeDirection" : true, "depth" : .330 * mm, "offsetDistance" : 25 * mm, "hasSecondDirection" : true, "secondDirectionOppositeDirection" : true, "secondDirectionDepth" : .150 * mm});
        }
    });
